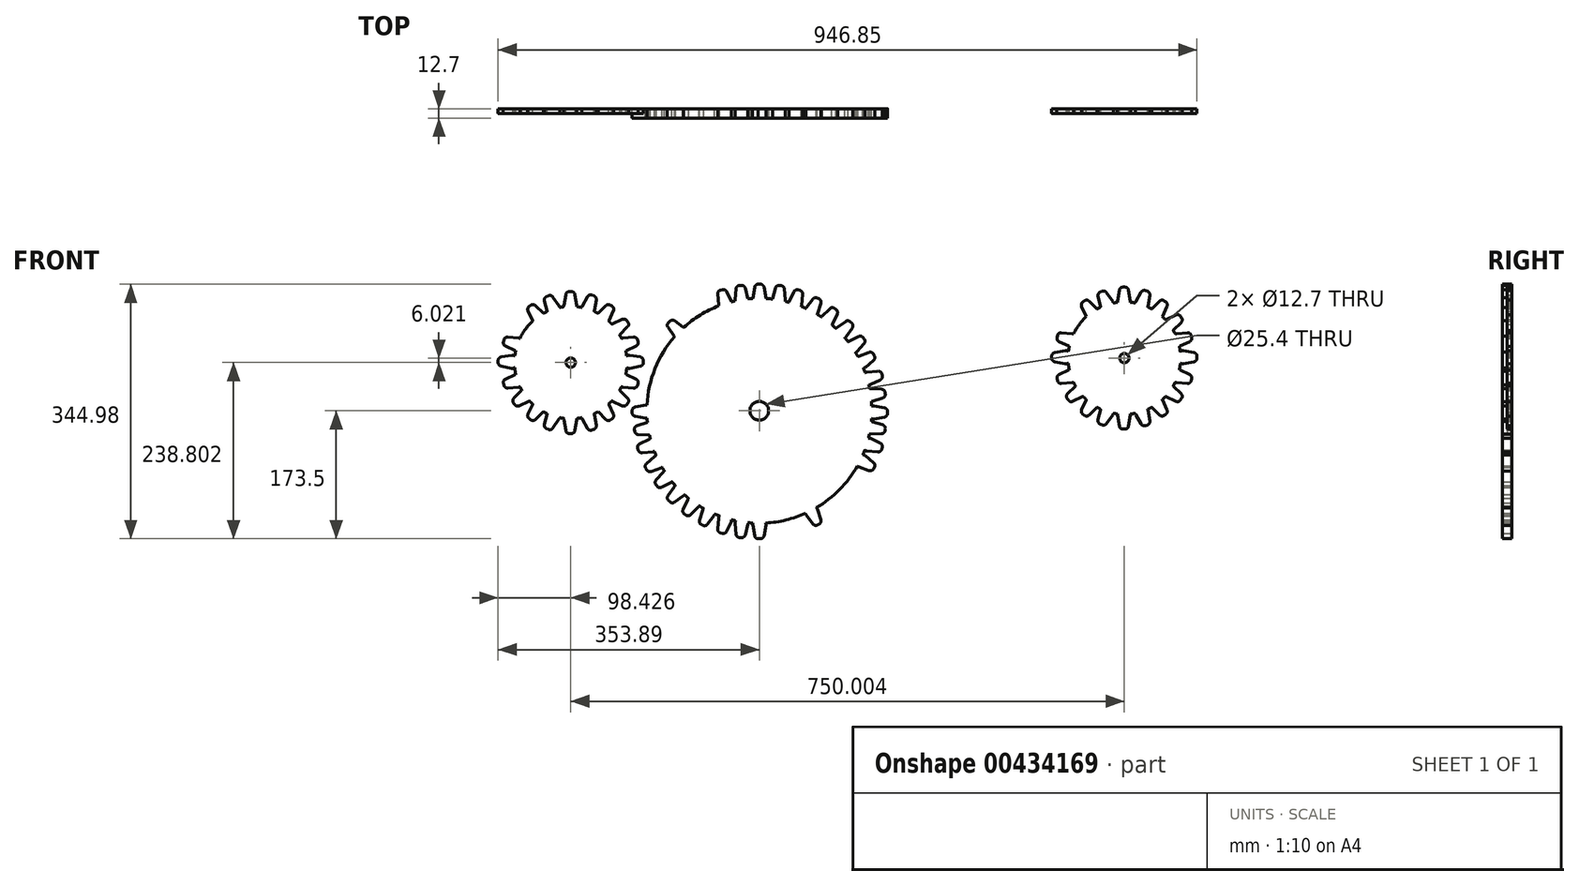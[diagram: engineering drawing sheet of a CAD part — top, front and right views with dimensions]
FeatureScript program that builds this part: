
annotation { "Feature Type Name" : "Feature", "Feature Type Description" : "" }
export const myFeature = defineFeature(function(context is Context, id is Id, definition is map)
    precondition{}
    {
        {
            var Q0;
            Q0=qCreatedBy(makeId("Front.planeOp"),FACE);
            var sketch = newSketch(context, id + "F0", { "sketchPlane" : qUnion([Q0])});
            skCircle(sketch, "E0", {"center": v(0, 0) * mm, "radius": 152.4 * mm});
            skCircle(sketch, "E1", {"center": v(0, 0) * mm, "radius": 12.7 * mm});
            skCircle(sketch, "E2", {"center": v(494.54, 71.32) * mm, "radius": 76.2 * mm});
            skCircle(sketch, "E3", {"center": v(494.54, 71.32) * mm, "radius": 6.35 * mm});
            skLineSegment(sketch, "E4", {"start": v(-3.93, 146.91) * mm, "end": v(3.69, 146.91) * mm});
            skLineSegment(sketch, "E5", {"start": v(-6.4, 167.28) * mm, "end": v(-8.94, 152.88) * mm});
            skPoint(sketch, "E6.visualSharp", {"position": v(5.4, 171.48) * mm});
            skPoint(sketch, "E7.visualSharp", {"position": v(-5.66, 171.48) * mm});
            skArc(sketch, "E7.filletArc", {"start": v(-1.37, 171.47) * mm, "mid": v(-4.65, 170.3) * mm, "end": v(-6.4, 167.28) * mm});
            skPoint(sketch, "E8.visualSharp", {"position": v(-9.99, 146.91) * mm});
            skArc(sketch, "E8.filletArc", {"start": v(-8.94, 152.88) * mm, "mid": v(-7.82, 148.73) * mm, "end": v(-3.93, 146.91) * mm});
            skPoint(sketch, "E9.visualSharp", {"position": v(9.74, 146.91) * mm});
            skLineSegment(sketch, "E10", {"start": v(10.44, 169.29) * mm, "end": v(10.23, 169.2) * mm});
            skPoint(sketch, "E11", {"position": v(18.24, 145.49) * mm});
            skLineSegment(sketch, "E12", {"start": v(22.3, 145.57) * mm, "end": v(29.9, 144.9) * mm});
            skLineSegment(sketch, "E13", {"start": v(35.4, 150.4) * mm, "end": v(34.12, 164.98) * mm});
            skLineSegment(sketch, "E14", {"start": v(29.5, 169.6) * mm, "end": v(26.98, 169.82) * mm});
            skLineSegment(sketch, "E15", {"start": v(21.63, 166.07) * mm, "end": v(17.84, 151.94) * mm});
            skArc(sketch, "E16.filletArc", {"start": v(34.12, 164.98) * mm, "mid": v(32.65, 168.13) * mm, "end": v(29.5, 169.6) * mm});
            skArc(sketch, "E17.filletArc", {"start": v(26.98, 169.82) * mm, "mid": v(23.62, 168.92) * mm, "end": v(21.63, 166.07) * mm});
            skArc(sketch, "E18.filletArc", {"start": v(17.84, 151.94) * mm, "mid": v(18.59, 147.71) * mm, "end": v(22.3, 145.57) * mm});
            skArc(sketch, "E19.filletArc", {"start": v(29.9, 144.9) * mm, "mid": v(33.93, 146.37) * mm, "end": v(35.4, 150.4) * mm});
            skLineSegment(sketch, "E20", {"start": v(43.8, 140.7) * mm, "end": v(51.17, 138.73) * mm});
            skLineSegment(sketch, "E21", {"start": v(57.54, 143.19) * mm, "end": v(58.82, 157.76) * mm});
            skLineSegment(sketch, "E22", {"start": v(55.07, 163.11) * mm, "end": v(52.62, 163.77) * mm});
            skLineSegment(sketch, "E23", {"start": v(46.7, 161) * mm, "end": v(40.52, 147.75) * mm});
            skArc(sketch, "E24.filletArc", {"start": v(58.82, 157.76) * mm, "mid": v(57.92, 161.12) * mm, "end": v(55.07, 163.11) * mm});
            skArc(sketch, "E25.filletArc", {"start": v(52.62, 163.77) * mm, "mid": v(49.16, 163.47) * mm, "end": v(46.7, 161) * mm});
            skArc(sketch, "E26.filletArc", {"start": v(40.52, 147.75) * mm, "mid": v(40.52, 143.46) * mm, "end": v(43.8, 140.7) * mm});
            skArc(sketch, "E27.filletArc", {"start": v(51.17, 138.73) * mm, "mid": v(55.4, 139.47) * mm, "end": v(57.54, 143.19) * mm});
            skLineSegment(sketch, "E28", {"start": v(65.39, 132.04) * mm, "end": v(71.8, 128.73) * mm});
            skLineSegment(sketch, "E29", {"start": v(78.98, 131.74) * mm, "end": v(83.32, 145.72) * mm});
            skLineSegment(sketch, "E30", {"start": v(80.79, 151.74) * mm, "end": v(78.89, 152.71) * mm});
            skLineSegment(sketch, "E31", {"start": v(72.52, 151.27) * mm, "end": v(63.67, 139.63) * mm});
            skArc(sketch, "E32.filletArc", {"start": v(83.32, 145.72) * mm, "mid": v(83.15, 149.19) * mm, "end": v(80.79, 151.74) * mm});
            skArc(sketch, "E33.filletArc", {"start": v(78.89, 152.71) * mm, "mid": v(75.44, 153.15) * mm, "end": v(72.52, 151.27) * mm});
            skArc(sketch, "E34.filletArc", {"start": v(63.67, 139.63) * mm, "mid": v(62.76, 135.43) * mm, "end": v(65.39, 132.04) * mm});
            skArc(sketch, "E35.filletArc", {"start": v(71.8, 128.73) * mm, "mid": v(76.1, 128.57) * mm, "end": v(78.98, 131.74) * mm});
            skLineSegment(sketch, "E36", {"start": v(85.6, 120.15) * mm, "end": v(91.84, 115.78) * mm});
            skLineSegment(sketch, "E37", {"start": v(99.36, 117.8) * mm, "end": v(105.54, 131.05) * mm});
            skLineSegment(sketch, "E38", {"start": v(103.85, 137.36) * mm, "end": v(101.77, 138.82) * mm});
            skLineSegment(sketch, "E39", {"start": v(95.26, 138.25) * mm, "end": v(84.92, 127.9) * mm});
            skArc(sketch, "E40.filletArc", {"start": v(105.54, 131.05) * mm, "mid": v(105.84, 134.51) * mm, "end": v(103.85, 137.36) * mm});
            skArc(sketch, "E41.filletArc", {"start": v(101.77, 138.82) * mm, "mid": v(98.41, 139.72) * mm, "end": v(95.26, 138.25) * mm});
            skArc(sketch, "E42.filletArc", {"start": v(84.92, 127.9) * mm, "mid": v(83.45, 123.87) * mm, "end": v(85.6, 120.15) * mm});
            skArc(sketch, "E43.filletArc", {"start": v(91.84, 115.78) * mm, "mid": v(96.07, 115.03) * mm, "end": v(99.36, 117.8) * mm});
            skLineSegment(sketch, "E44", {"start": v(104.46, 105.05) * mm, "end": v(109.86, 99.65) * mm});
            skLineSegment(sketch, "E45", {"start": v(117.62, 100.33) * mm, "end": v(125.88, 112.13) * mm});
            skLineSegment(sketch, "E46", {"start": v(125.31, 118.63) * mm, "end": v(123.45, 120.5) * mm});
            skLineSegment(sketch, "E47", {"start": v(116.94, 121.06) * mm, "end": v(105.14, 112.8) * mm});
            skArc(sketch, "E48.filletArc", {"start": v(125.88, 112.13) * mm, "mid": v(126.78, 115.48) * mm, "end": v(125.31, 118.63) * mm});
            skArc(sketch, "E49.filletArc", {"start": v(123.45, 120.5) * mm, "mid": v(120.3, 121.96) * mm, "end": v(116.94, 121.06) * mm});
            skArc(sketch, "E50.filletArc", {"start": v(105.14, 112.8) * mm, "mid": v(103, 109.08) * mm, "end": v(104.46, 105.05) * mm});
            skArc(sketch, "E51.filletArc", {"start": v(109.86, 99.65) * mm, "mid": v(113.9, 98.18) * mm, "end": v(117.62, 100.33) * mm});
            skLineSegment(sketch, "E52", {"start": v(119.6, 86.31) * mm, "end": v(124.28, 80.3) * mm});
            skLineSegment(sketch, "E53", {"start": v(132.05, 80) * mm, "end": v(141.88, 90.84) * mm});
            skLineSegment(sketch, "E54", {"start": v(142.12, 97.37) * mm, "end": v(140.57, 99.37) * mm});
            skLineSegment(sketch, "E55", {"start": v(134.18, 100.75) * mm, "end": v(121.25, 93.92) * mm});
            skArc(sketch, "E56.filletArc", {"start": v(141.88, 90.84) * mm, "mid": v(143.19, 94.06) * mm, "end": v(142.12, 97.37) * mm});
            skArc(sketch, "E57.filletArc", {"start": v(140.57, 99.37) * mm, "mid": v(137.62, 101.22) * mm, "end": v(134.18, 100.75) * mm});
            skArc(sketch, "E58.filletArc", {"start": v(121.25, 93.92) * mm, "mid": v(118.65, 90.5) * mm, "end": v(119.6, 86.31) * mm});
            skArc(sketch, "E59.filletArc", {"start": v(124.28, 80.3) * mm, "mid": v(128.1, 78.33) * mm, "end": v(132.05, 80) * mm});
            skLineSegment(sketch, "E60", {"start": v(132.03, 66.8) * mm, "end": v(135.84, 60.2) * mm});
            skLineSegment(sketch, "E61", {"start": v(143.5, 58.84) * mm, "end": v(154.71, 68.24) * mm});
            skLineSegment(sketch, "E62", {"start": v(155.85, 74.68) * mm, "end": v(154.58, 76.88) * mm});
            skLineSegment(sketch, "E63", {"start": v(148.44, 79.1) * mm, "end": v(134.7, 74.1) * mm});
            skArc(sketch, "E64.filletArc", {"start": v(154.71, 68.24) * mm, "mid": v(156.45, 71.25) * mm, "end": v(155.85, 74.68) * mm});
            skArc(sketch, "E65.filletArc", {"start": v(154.58, 76.88) * mm, "mid": v(151.92, 79.1) * mm, "end": v(148.44, 79.1) * mm});
            skArc(sketch, "E66.filletArc", {"start": v(134.7, 74.1) * mm, "mid": v(131.66, 71.07) * mm, "end": v(132.03, 66.8) * mm});
            skArc(sketch, "E67.filletArc", {"start": v(135.84, 60.2) * mm, "mid": v(139.36, 57.73) * mm, "end": v(143.5, 58.84) * mm});
            skLineSegment(sketch, "E68", {"start": v(141.48, 46.14) * mm, "end": v(143.45, 38.78) * mm});
            skLineSegment(sketch, "E69", {"start": v(150.5, 35.5) * mm, "end": v(163.76, 41.68) * mm});
            skLineSegment(sketch, "E70", {"start": v(166.52, 47.6) * mm, "end": v(165.86, 50.05) * mm});
            skLineSegment(sketch, "E71", {"start": v(160.51, 53.8) * mm, "end": v(145.94, 52.52) * mm});
            skArc(sketch, "E72.filletArc", {"start": v(163.76, 41.68) * mm, "mid": v(166.22, 44.13) * mm, "end": v(166.52, 47.6) * mm});
            skArc(sketch, "E73.filletArc", {"start": v(165.86, 50.05) * mm, "mid": v(163.87, 52.9) * mm, "end": v(160.51, 53.8) * mm});
            skArc(sketch, "E74.filletArc", {"start": v(145.94, 52.52) * mm, "mid": v(142.22, 50.37) * mm, "end": v(141.48, 46.14) * mm});
            skArc(sketch, "E75.filletArc", {"start": v(143.45, 38.78) * mm, "mid": v(146.2, 35.5) * mm, "end": v(150.5, 35.5) * mm});
            skLineSegment(sketch, "E76", {"start": v(145.77, 24.1) * mm, "end": v(146.7, 16.95) * mm});
            skLineSegment(sketch, "E77", {"start": v(153.25, 12.76) * mm, "end": v(167.2, 17.14) * mm});
            skLineSegment(sketch, "E78", {"start": v(170.73, 22.64) * mm, "end": v(170.45, 24.74) * mm});
            skLineSegment(sketch, "E79", {"start": v(165.65, 29.16) * mm, "end": v(151.03, 29.82) * mm});
            skArc(sketch, "E80.filletArc", {"start": v(167.2, 17.14) * mm, "mid": v(169.97, 19.25) * mm, "end": v(170.73, 22.64) * mm});
            skArc(sketch, "E81.filletArc", {"start": v(170.45, 24.74) * mm, "mid": v(168.85, 27.83) * mm, "end": v(165.65, 29.16) * mm});
            skArc(sketch, "E82.filletArc", {"start": v(151.03, 29.82) * mm, "mid": v(147.06, 28.18) * mm, "end": v(145.77, 24.1) * mm});
            skArc(sketch, "E83.filletArc", {"start": v(146.7, 16.95) * mm, "mid": v(149, 13.33) * mm, "end": v(153.25, 12.76) * mm});
            skLineSegment(sketch, "E84.MirrorCS", {"start": v(-1.37, 171.47) * mm, "end": v(1.4, 171.48) * mm});
            skLineSegment(sketch, "E85.MirrorCS", {"start": v(-10.44, 169.29) * mm, "end": v(-10.23, 169.2) * mm});
            skLineSegment(sketch, "E86.MirrorCS", {"start": v(3.93, 146.91) * mm, "end": v(-3.69, 146.91) * mm});
            skLineSegment(sketch, "E87.MirrorCS", {"start": v(6.4, 167.28) * mm, "end": v(8.94, 152.88) * mm});
            skArc(sketch, "E88.MirrorCS", {"start": v(1.4, 171.48) * mm, "mid": v(4.66, 170.29) * mm, "end": v(6.4, 167.28) * mm});
            skArc(sketch, "E89.MirrorCS", {"start": v(8.94, 152.88) * mm, "mid": v(7.82, 148.73) * mm, "end": v(3.93, 146.91) * mm});
            skPoint(sketch, "E90.MirrorP", {"position": v(-5.4, 171.48) * mm});
            skPoint(sketch, "E91.MirrorP", {"position": v(5.66, 171.48) * mm});
            skPoint(sketch, "E92.MirrorP", {"position": v(9.99, 146.91) * mm});
            skPoint(sketch, "E93.MirrorP", {"position": v(-9.74, 146.91) * mm});
            skLineSegment(sketch, "E94", {"start": v(149.19, 1.53) * mm, "end": v(149.19, -6.1) * mm});
            skLineSegment(sketch, "E95", {"start": v(155.15, -11.1) * mm, "end": v(169.56, -8.56) * mm});
            skLineSegment(sketch, "E96", {"start": v(173.75, -3.55) * mm, "end": v(173.75, -1.01) * mm});
            skLineSegment(sketch, "E97", {"start": v(169.56, 4) * mm, "end": v(155.15, 6.53) * mm});
            skArc(sketch, "E98.filletArc", {"start": v(169.56, -8.56) * mm, "mid": v(172.57, -6.82) * mm, "end": v(173.75, -3.55) * mm});
            skArc(sketch, "E99.filletArc", {"start": v(173.75, -1.01) * mm, "mid": v(172.57, 2.25) * mm, "end": v(169.56, 4) * mm});
            skArc(sketch, "E100.filletArc", {"start": v(155.15, 6.53) * mm, "mid": v(151, 5.42) * mm, "end": v(149.19, 1.53) * mm});
            skArc(sketch, "E101.filletArc", {"start": v(149.19, -6.1) * mm, "mid": v(151, -9.98) * mm, "end": v(155.15, -11.1) * mm});
            skLineSegment(sketch, "E102", {"start": v(494.54, 185.24) * mm, "end": v(494.54, -63.97) * mm});
            skLineSegment(sketch, "E103", {"start": v(395, 71.32) * mm, "end": v(592.82, 71.32) * mm});
            skLineSegment(sketch, "E104", {"start": v(490.18, 142.96) * mm, "end": v(497.8, 142.96) * mm});
            skLineSegment(sketch, "E105", {"start": v(502.8, 148.92) * mm, "end": v(500.26, 163.33) * mm});
            skLineSegment(sketch, "E106", {"start": v(495.26, 167.52) * mm, "end": v(492.72, 167.52) * mm});
            skLineSegment(sketch, "E107", {"start": v(487.72, 163.33) * mm, "end": v(485.18, 148.92) * mm});
            skArc(sketch, "E108.filletArc", {"start": v(500.26, 163.33) * mm, "mid": v(498.52, 166.34) * mm, "end": v(495.26, 167.52) * mm});
            skArc(sketch, "E109.filletArc", {"start": v(492.72, 167.52) * mm, "mid": v(489.45, 166.34) * mm, "end": v(487.72, 163.33) * mm});
            skArc(sketch, "E110.filletArc", {"start": v(485.18, 148.92) * mm, "mid": v(486.29, 144.77) * mm, "end": v(490.18, 142.96) * mm});
            skArc(sketch, "E111.filletArc", {"start": v(497.8, 142.96) * mm, "mid": v(501.69, 144.77) * mm, "end": v(502.8, 148.92) * mm});
            skLineSegment(sketch, "E112", {"start": v(512.62, 140.59) * mm, "end": v(519.78, 137.98) * mm});
            skLineSegment(sketch, "E113", {"start": v(526.52, 141.87) * mm, "end": v(529.06, 156.28) * mm});
            skLineSegment(sketch, "E114", {"start": v(525.8, 161.93) * mm, "end": v(523.4, 162.8) * mm});
            skLineSegment(sketch, "E115", {"start": v(517.27, 160.57) * mm, "end": v(509.95, 147.9) * mm});
            skArc(sketch, "E116.filletArc", {"start": v(529.06, 156.28) * mm, "mid": v(528.45, 159.7) * mm, "end": v(525.8, 161.93) * mm});
            skArc(sketch, "E117.filletArc", {"start": v(523.4, 162.8) * mm, "mid": v(519.93, 162.8) * mm, "end": v(517.27, 160.57) * mm});
            skArc(sketch, "E118.filletArc", {"start": v(509.95, 147.9) * mm, "mid": v(509.58, 143.62) * mm, "end": v(512.62, 140.59) * mm});
            skArc(sketch, "E119.filletArc", {"start": v(519.78, 137.98) * mm, "mid": v(524.05, 138.35) * mm, "end": v(526.52, 141.87) * mm});
            skLineSegment(sketch, "E120", {"start": v(532.43, 130.27) * mm, "end": v(538.67, 125.9) * mm});
            skLineSegment(sketch, "E121", {"start": v(546.2, 127.91) * mm, "end": v(552.37, 141.17) * mm});
            skLineSegment(sketch, "E122", {"start": v(550.68, 147.48) * mm, "end": v(548.6, 148.94) * mm});
            skLineSegment(sketch, "E123", {"start": v(542.1, 148.37) * mm, "end": v(531.75, 138.02) * mm});
            skArc(sketch, "E124.filletArc", {"start": v(552.37, 141.17) * mm, "mid": v(552.68, 144.63) * mm, "end": v(550.68, 147.48) * mm});
            skArc(sketch, "E125.filletArc", {"start": v(548.6, 148.94) * mm, "mid": v(545.25, 149.84) * mm, "end": v(542.1, 148.37) * mm});
            skArc(sketch, "E126.filletArc", {"start": v(531.75, 138.02) * mm, "mid": v(530.29, 133.99) * mm, "end": v(532.43, 130.27) * mm});
            skArc(sketch, "E127.filletArc", {"start": v(538.67, 125.9) * mm, "mid": v(542.9, 125.15) * mm, "end": v(546.2, 127.91) * mm});
            skLineSegment(sketch, "E128", {"start": v(549.03, 116.13) * mm, "end": v(553.4, 109.89) * mm});
            skLineSegment(sketch, "E129", {"start": v(561.15, 109.2) * mm, "end": v(571.5, 119.55) * mm});
            skLineSegment(sketch, "E130", {"start": v(572.06, 126.06) * mm, "end": v(570.6, 128.14) * mm});
            skLineSegment(sketch, "E131", {"start": v(564.3, 129.83) * mm, "end": v(551.04, 123.64) * mm});
            skArc(sketch, "E132.filletArc", {"start": v(571.5, 119.55) * mm, "mid": v(572.96, 122.7) * mm, "end": v(572.06, 126.06) * mm});
            skArc(sketch, "E133.filletArc", {"start": v(570.6, 128.14) * mm, "mid": v(567.76, 130.13) * mm, "end": v(564.3, 129.83) * mm});
            skArc(sketch, "E134.filletArc", {"start": v(551.04, 123.64) * mm, "mid": v(548.28, 120.36) * mm, "end": v(549.03, 116.13) * mm});
            skArc(sketch, "E135.filletArc", {"start": v(553.4, 109.89) * mm, "mid": v(557.12, 107.74) * mm, "end": v(561.15, 109.2) * mm});
            skLineSegment(sketch, "E136", {"start": v(560.7, 98.14) * mm, "end": v(562.67, 90.78) * mm});
            skLineSegment(sketch, "E137", {"start": v(569.73, 87.5) * mm, "end": v(582.98, 93.68) * mm});
            skLineSegment(sketch, "E138", {"start": v(585.74, 99.6) * mm, "end": v(585.09, 102.05) * mm});
            skLineSegment(sketch, "E139", {"start": v(579.74, 105.8) * mm, "end": v(565.17, 104.52) * mm});
            skArc(sketch, "E140.filletArc", {"start": v(582.98, 93.68) * mm, "mid": v(585.44, 96.13) * mm, "end": v(585.74, 99.6) * mm});
            skArc(sketch, "E141.filletArc", {"start": v(585.09, 102.05) * mm, "mid": v(583.1, 104.9) * mm, "end": v(579.74, 105.8) * mm});
            skArc(sketch, "E142.filletArc", {"start": v(565.17, 104.52) * mm, "mid": v(561.45, 102.37) * mm, "end": v(560.7, 98.14) * mm});
            skArc(sketch, "E143.filletArc", {"start": v(562.67, 90.78) * mm, "mid": v(565.43, 87.5) * mm, "end": v(569.73, 87.5) * mm});
            skLineSegment(sketch, "E144", {"start": v(568.33, 76.14) * mm, "end": v(568.44, 68.52) * mm});
            skLineSegment(sketch, "E145", {"start": v(574.47, 63.6) * mm, "end": v(588.84, 66.35) * mm});
            skLineSegment(sketch, "E146", {"start": v(592.96, 71.41) * mm, "end": v(592.93, 73.95) * mm});
            skLineSegment(sketch, "E147", {"start": v(588.66, 78.9) * mm, "end": v(574.22, 81.23) * mm});
            skArc(sketch, "E148.filletArc", {"start": v(588.84, 66.35) * mm, "mid": v(591.82, 68.13) * mm, "end": v(592.96, 71.41) * mm});
            skArc(sketch, "E149.filletArc", {"start": v(592.93, 73.95) * mm, "mid": v(591.7, 77.2) * mm, "end": v(588.66, 78.9) * mm});
            skArc(sketch, "E150.filletArc", {"start": v(574.22, 81.23) * mm, "mid": v(570.09, 80.06) * mm, "end": v(568.33, 76.14) * mm});
            skArc(sketch, "E151.filletArc", {"start": v(568.44, 68.52) * mm, "mid": v(570.3, 64.66) * mm, "end": v(574.47, 63.6) * mm});
            skLineSegment(sketch, "E152.MirrorCS", {"start": v(396.12, 71.41) * mm, "end": v(396.15, 73.95) * mm});
            skLineSegment(sketch, "E153.MirrorCS", {"start": v(403.34, 99.6) * mm, "end": v(404, 102.05) * mm});
            skArc(sketch, "E154.MirrorCS", {"start": v(396.15, 73.95) * mm, "mid": v(397.39, 77.2) * mm, "end": v(400.42, 78.9) * mm});
            skArc(sketch, "E155.MirrorCS", {"start": v(418.47, 128.14) * mm, "mid": v(421.32, 130.13) * mm, "end": v(424.78, 129.83) * mm});
            skArc(sketch, "E156.MirrorCS", {"start": v(414.86, 81.23) * mm, "mid": v(419, 80.06) * mm, "end": v(420.75, 76.14) * mm});
            skArc(sketch, "E157.MirrorCS", {"start": v(438.04, 123.64) * mm, "mid": v(440.8, 120.36) * mm, "end": v(440.05, 116.13) * mm});
            skArc(sketch, "E158.MirrorCS", {"start": v(435.68, 109.89) * mm, "mid": v(431.96, 107.74) * mm, "end": v(427.93, 109.2) * mm});
            skLineSegment(sketch, "E159.MirrorCS", {"start": v(456.65, 130.27) * mm, "end": v(450.4, 125.9) * mm});
            skLineSegment(sketch, "E160.MirrorCS", {"start": v(428.38, 98.14) * mm, "end": v(426.4, 90.78) * mm});
            skLineSegment(sketch, "E161.MirrorCS", {"start": v(438.4, 147.48) * mm, "end": v(440.48, 148.94) * mm});
            skArc(sketch, "E162.MirrorCS", {"start": v(406.1, 93.68) * mm, "mid": v(403.64, 96.13) * mm, "end": v(403.34, 99.6) * mm});
            skArc(sketch, "E163.MirrorCS", {"start": v(436.7, 141.17) * mm, "mid": v(436.4, 144.63) * mm, "end": v(438.4, 147.48) * mm});
            skArc(sketch, "E164.MirrorCS", {"start": v(404, 102.05) * mm, "mid": v(405.99, 104.9) * mm, "end": v(409.34, 105.8) * mm});
            skArc(sketch, "E165.MirrorCS", {"start": v(440.48, 148.94) * mm, "mid": v(443.83, 149.84) * mm, "end": v(446.98, 148.37) * mm});
            skArc(sketch, "E166.MirrorCS", {"start": v(457.33, 138.02) * mm, "mid": v(458.8, 133.99) * mm, "end": v(456.65, 130.27) * mm});
            skArc(sketch, "E167.MirrorCS", {"start": v(423.91, 104.52) * mm, "mid": v(427.63, 102.37) * mm, "end": v(428.38, 98.14) * mm});
            skArc(sketch, "E168.MirrorCS", {"start": v(450.4, 125.9) * mm, "mid": v(446.18, 125.15) * mm, "end": v(442.89, 127.91) * mm});
            skArc(sketch, "E169.MirrorCS", {"start": v(426.4, 90.78) * mm, "mid": v(423.65, 87.5) * mm, "end": v(419.35, 87.5) * mm});
            skLineSegment(sketch, "E170.MirrorCS", {"start": v(440.05, 116.13) * mm, "end": v(435.68, 109.89) * mm});
            skLineSegment(sketch, "E171.MirrorCS", {"start": v(420.75, 76.14) * mm, "end": v(420.64, 68.52) * mm});
            skLineSegment(sketch, "E172.MirrorCS", {"start": v(417.02, 126.06) * mm, "end": v(418.47, 128.14) * mm});
            skArc(sketch, "E173.MirrorCS", {"start": v(417.58, 119.55) * mm, "mid": v(416.12, 122.7) * mm, "end": v(417.02, 126.06) * mm});
            skArc(sketch, "E174.MirrorCS", {"start": v(400.24, 66.35) * mm, "mid": v(397.26, 68.13) * mm, "end": v(396.12, 71.41) * mm});
            skLineSegment(sketch, "E175.MirrorCS", {"start": v(424.78, 129.83) * mm, "end": v(438.04, 123.64) * mm});
            skLineSegment(sketch, "E176.MirrorCS", {"start": v(400.42, 78.9) * mm, "end": v(414.86, 81.23) * mm});
            skArc(sketch, "E177.MirrorCS", {"start": v(420.64, 68.52) * mm, "mid": v(418.77, 64.66) * mm, "end": v(414.61, 63.6) * mm});
            skLineSegment(sketch, "E178.MirrorCS", {"start": v(419.35, 87.5) * mm, "end": v(406.1, 93.68) * mm});
            skLineSegment(sketch, "E179.MirrorCS", {"start": v(442.89, 127.91) * mm, "end": v(436.7, 141.17) * mm});
            skLineSegment(sketch, "E180.MirrorCS", {"start": v(409.34, 105.8) * mm, "end": v(423.91, 104.52) * mm});
            skLineSegment(sketch, "E181.MirrorCS", {"start": v(446.98, 148.37) * mm, "end": v(457.33, 138.02) * mm});
            skLineSegment(sketch, "E182.MirrorCS", {"start": v(427.93, 109.2) * mm, "end": v(417.58, 119.55) * mm});
            skLineSegment(sketch, "E183.MirrorCS", {"start": v(414.61, 63.6) * mm, "end": v(400.24, 66.35) * mm});
            skLineSegment(sketch, "E184", {"start": v(469.82, 137.42) * mm, "end": v(476.73, 140.64) * mm});
            skLineSegment(sketch, "E185", {"start": v(478.74, 148.16) * mm, "end": v(470.35, 160.14) * mm});
            skLineSegment(sketch, "E186", {"start": v(464.04, 161.83) * mm, "end": v(461.74, 160.76) * mm});
            skLineSegment(sketch, "E187", {"start": v(458.98, 154.84) * mm, "end": v(462.77, 140.71) * mm});
            skArc(sketch, "E188.filletArc", {"start": v(470.35, 160.14) * mm, "mid": v(467.5, 162.14) * mm, "end": v(464.04, 161.83) * mm});
            skArc(sketch, "E189.filletArc", {"start": v(461.74, 160.76) * mm, "mid": v(459.28, 158.3) * mm, "end": v(458.98, 154.84) * mm});
            skArc(sketch, "E190.filletArc", {"start": v(462.77, 140.71) * mm, "mid": v(465.53, 137.42) * mm, "end": v(469.82, 137.42) * mm});
            skArc(sketch, "E191.filletArc", {"start": v(476.73, 140.64) * mm, "mid": v(479.49, 143.93) * mm, "end": v(478.74, 148.16) * mm});
            skLineSegment(sketch, "E192.MirrorCS", {"start": v(403.34, 43.05) * mm, "end": v(404, 40.6) * mm});
            skLineSegment(sketch, "E193.MirrorCS", {"start": v(585.74, 43.05) * mm, "end": v(585.09, 40.6) * mm});
            skLineSegment(sketch, "E194.MirrorCS", {"start": v(550.68, -4.83) * mm, "end": v(548.6, -6.3) * mm});
            skLineSegment(sketch, "E195.MirrorCS", {"start": v(495.26, -24.88) * mm, "end": v(492.72, -24.88) * mm});
            skLineSegment(sketch, "E196.MirrorCS", {"start": v(464.04, -19.19) * mm, "end": v(461.74, -18.11) * mm});
            skLineSegment(sketch, "E197.MirrorCS", {"start": v(417.02, 16.6) * mm, "end": v(418.47, 14.51) * mm});
            skLineSegment(sketch, "E198.MirrorCS", {"start": v(438.4, -4.83) * mm, "end": v(440.48, -6.3) * mm});
            skLineSegment(sketch, "E199.MirrorCS", {"start": v(572.06, 16.6) * mm, "end": v(570.6, 14.51) * mm});
            skLineSegment(sketch, "E200.MirrorCS", {"start": v(525.8, -19.29) * mm, "end": v(523.4, -20.15) * mm});
            skArc(sketch, "E201.MirrorCS", {"start": v(582.98, 48.97) * mm, "mid": v(585.44, 46.51) * mm, "end": v(585.74, 43.05) * mm});
            skArc(sketch, "E202.MirrorCS", {"start": v(571.5, 23.1) * mm, "mid": v(572.96, 19.95) * mm, "end": v(572.06, 16.6) * mm});
            skArc(sketch, "E203.MirrorCS", {"start": v(519.78, 4.67) * mm, "mid": v(524.05, 4.3) * mm, "end": v(526.52, 0.78) * mm});
            skArc(sketch, "E204.MirrorCS", {"start": v(423.91, 38.13) * mm, "mid": v(427.63, 40.27) * mm, "end": v(428.38, 44.5) * mm});
            skArc(sketch, "E205.MirrorCS", {"start": v(553.4, 32.76) * mm, "mid": v(557.12, 34.9) * mm, "end": v(561.15, 33.44) * mm});
            skLineSegment(sketch, "E206.MirrorCS", {"start": v(560.7, 44.5) * mm, "end": v(562.67, 51.86) * mm});
            skLineSegment(sketch, "E207.MirrorCS", {"start": v(532.43, 12.38) * mm, "end": v(538.67, 16.75) * mm});
            skLineSegment(sketch, "E208.MirrorCS", {"start": v(490.18, -0.31) * mm, "end": v(497.8, -0.31) * mm});
            skArc(sketch, "E209.MirrorCS", {"start": v(450.4, 16.75) * mm, "mid": v(446.18, 17.5) * mm, "end": v(442.89, 14.73) * mm});
            skLineSegment(sketch, "E210.MirrorCS", {"start": v(469.82, 5.22) * mm, "end": v(476.73, 2) * mm});
            skLineSegment(sketch, "E211.MirrorCS", {"start": v(569.73, 55.15) * mm, "end": v(582.98, 48.97) * mm});
            skLineSegment(sketch, "E212.MirrorCS", {"start": v(546.2, 14.73) * mm, "end": v(552.37, 1.47) * mm});
            skLineSegment(sketch, "E213.MirrorCS", {"start": v(502.8, -6.27) * mm, "end": v(500.26, -20.68) * mm});
            skLineSegment(sketch, "E214.MirrorCS", {"start": v(478.74, -5.51) * mm, "end": v(470.35, -17.5) * mm});
            skArc(sketch, "E215.MirrorCS", {"start": v(426.4, 51.86) * mm, "mid": v(423.65, 55.15) * mm, "end": v(419.35, 55.15) * mm});
            skLineSegment(sketch, "E216.MirrorCS", {"start": v(440.05, 26.52) * mm, "end": v(435.68, 32.76) * mm});
            skArc(sketch, "E217.MirrorCS", {"start": v(418.47, 14.51) * mm, "mid": v(421.32, 12.52) * mm, "end": v(424.78, 12.82) * mm});
            skLineSegment(sketch, "E218.MirrorCS", {"start": v(579.74, 36.85) * mm, "end": v(565.17, 38.13) * mm});
            skLineSegment(sketch, "E219.MirrorCS", {"start": v(542.1, -5.72) * mm, "end": v(531.75, 4.62) * mm});
            skLineSegment(sketch, "E220.MirrorCS", {"start": v(487.72, -20.68) * mm, "end": v(485.18, -6.27) * mm});
            skLineSegment(sketch, "E221.MirrorCS", {"start": v(458.98, -12.2) * mm, "end": v(462.77, 1.93) * mm});
            skArc(sketch, "E222.MirrorCS", {"start": v(470.35, -17.5) * mm, "mid": v(467.5, -19.49) * mm, "end": v(464.04, -19.19) * mm});
            skArc(sketch, "E223.MirrorCS", {"start": v(552.37, 1.47) * mm, "mid": v(552.68, -1.99) * mm, "end": v(550.68, -4.83) * mm});
            skArc(sketch, "E224.MirrorCS", {"start": v(500.26, -20.68) * mm, "mid": v(498.52, -23.69) * mm, "end": v(495.26, -24.88) * mm});
            skArc(sketch, "E225.MirrorCS", {"start": v(461.74, -18.11) * mm, "mid": v(459.28, -15.66) * mm, "end": v(458.98, -12.2) * mm});
            skArc(sketch, "E226.MirrorCS", {"start": v(417.58, 23.1) * mm, "mid": v(416.12, 19.95) * mm, "end": v(417.02, 16.6) * mm});
            skArc(sketch, "E227.MirrorCS", {"start": v(438.04, 19) * mm, "mid": v(440.8, 22.3) * mm, "end": v(440.05, 26.52) * mm});
            skArc(sketch, "E228.MirrorCS", {"start": v(585.09, 40.6) * mm, "mid": v(583.1, 37.75) * mm, "end": v(579.74, 36.85) * mm});
            skArc(sketch, "E229.MirrorCS", {"start": v(548.6, -6.3) * mm, "mid": v(545.25, -7.19) * mm, "end": v(542.1, -5.72) * mm});
            skArc(sketch, "E230.MirrorCS", {"start": v(492.72, -24.88) * mm, "mid": v(489.45, -23.69) * mm, "end": v(487.72, -20.68) * mm});
            skArc(sketch, "E231.MirrorCS", {"start": v(531.75, 4.62) * mm, "mid": v(530.29, 8.66) * mm, "end": v(532.43, 12.38) * mm});
            skArc(sketch, "E232.MirrorCS", {"start": v(485.18, -6.27) * mm, "mid": v(486.29, -2.13) * mm, "end": v(490.18, -0.31) * mm});
            skArc(sketch, "E233.MirrorCS", {"start": v(435.68, 32.76) * mm, "mid": v(431.96, 34.9) * mm, "end": v(427.93, 33.44) * mm});
            skArc(sketch, "E234.MirrorCS", {"start": v(462.77, 1.93) * mm, "mid": v(465.53, 5.22) * mm, "end": v(469.82, 5.22) * mm});
            skArc(sketch, "E235.MirrorCS", {"start": v(565.17, 38.13) * mm, "mid": v(561.45, 40.27) * mm, "end": v(560.7, 44.5) * mm});
            skArc(sketch, "E236.MirrorCS", {"start": v(538.67, 16.75) * mm, "mid": v(542.9, 17.5) * mm, "end": v(546.2, 14.73) * mm});
            skArc(sketch, "E237.MirrorCS", {"start": v(497.8, -0.31) * mm, "mid": v(501.69, -2.13) * mm, "end": v(502.8, -6.27) * mm});
            skLineSegment(sketch, "E238.MirrorCS", {"start": v(456.65, 12.38) * mm, "end": v(450.4, 16.75) * mm});
            skArc(sketch, "E239.MirrorCS", {"start": v(562.67, 51.86) * mm, "mid": v(565.43, 55.15) * mm, "end": v(569.73, 55.15) * mm});
            skLineSegment(sketch, "E240.MirrorCS", {"start": v(424.78, 12.82) * mm, "end": v(438.04, 19) * mm});
            skArc(sketch, "E241.MirrorCS", {"start": v(476.73, 2) * mm, "mid": v(479.49, -1.29) * mm, "end": v(478.74, -5.51) * mm});
            skLineSegment(sketch, "E242.MirrorCS", {"start": v(549.03, 26.52) * mm, "end": v(553.4, 32.76) * mm});
            skLineSegment(sketch, "E243.MirrorCS", {"start": v(512.62, 2.06) * mm, "end": v(519.78, 4.67) * mm});
            skLineSegment(sketch, "E244.MirrorCS", {"start": v(428.38, 44.5) * mm, "end": v(426.4, 51.86) * mm});
            skLineSegment(sketch, "E245.MirrorCS", {"start": v(561.15, 33.44) * mm, "end": v(571.5, 23.1) * mm});
            skLineSegment(sketch, "E246.MirrorCS", {"start": v(526.52, 0.78) * mm, "end": v(529.06, -13.63) * mm});
            skArc(sketch, "E247.MirrorCS", {"start": v(406.1, 48.97) * mm, "mid": v(403.64, 46.51) * mm, "end": v(403.34, 43.05) * mm});
            skLineSegment(sketch, "E248.MirrorCS", {"start": v(419.35, 55.15) * mm, "end": v(406.1, 48.97) * mm});
            skLineSegment(sketch, "E249.MirrorCS", {"start": v(564.3, 12.82) * mm, "end": v(551.04, 19) * mm});
            skLineSegment(sketch, "E250.MirrorCS", {"start": v(517.27, -17.92) * mm, "end": v(509.95, -5.25) * mm});
            skArc(sketch, "E251.MirrorCS", {"start": v(436.7, 1.47) * mm, "mid": v(436.4, -1.99) * mm, "end": v(438.4, -4.83) * mm});
            skLineSegment(sketch, "E252.MirrorCS", {"start": v(442.89, 14.73) * mm, "end": v(436.7, 1.47) * mm});
            skArc(sketch, "E253.MirrorCS", {"start": v(551.04, 19) * mm, "mid": v(548.28, 22.3) * mm, "end": v(549.03, 26.52) * mm});
            skArc(sketch, "E254.MirrorCS", {"start": v(509.95, -5.25) * mm, "mid": v(509.58, -0.98) * mm, "end": v(512.62, 2.06) * mm});
            skArc(sketch, "E255.MirrorCS", {"start": v(570.6, 14.51) * mm, "mid": v(567.76, 12.52) * mm, "end": v(564.3, 12.82) * mm});
            skArc(sketch, "E256.MirrorCS", {"start": v(523.4, -20.15) * mm, "mid": v(519.93, -20.15) * mm, "end": v(517.27, -17.92) * mm});
            skLineSegment(sketch, "E257.MirrorCS", {"start": v(427.93, 33.44) * mm, "end": v(417.58, 23.1) * mm});
            skLineSegment(sketch, "E258.MirrorCS", {"start": v(446.98, -5.72) * mm, "end": v(457.33, 4.62) * mm});
            skArc(sketch, "E259.MirrorCS", {"start": v(440.48, -6.3) * mm, "mid": v(443.83, -7.19) * mm, "end": v(446.98, -5.72) * mm});
            skLineSegment(sketch, "E260.MirrorCS", {"start": v(409.34, 36.85) * mm, "end": v(423.91, 38.13) * mm});
            skArc(sketch, "E261.MirrorCS", {"start": v(529.06, -13.63) * mm, "mid": v(528.45, -17.05) * mm, "end": v(525.8, -19.29) * mm});
            skArc(sketch, "E262.MirrorCS", {"start": v(404, 40.6) * mm, "mid": v(405.99, 37.75) * mm, "end": v(409.34, 36.85) * mm});
            skArc(sketch, "E263.MirrorCS", {"start": v(457.33, 4.62) * mm, "mid": v(458.8, 8.66) * mm, "end": v(456.65, 12.38) * mm});
            skPoint(sketch, "E264.endSnap0", {"position": v(0.12, 146.91) * mm});
            skArc(sketch, "E265.MirrorCS", {"start": v(-103.23, 131.73) * mm, "mid": v(-103.51, 135.2) * mm, "end": v(-101.5, 138.03) * mm});
            skLineSegment(sketch, "E266.MirrorCS", {"start": v(-123.09, 119.44) * mm, "end": v(-121.21, 121.3) * mm});
            skLineSegment(sketch, "E267.MirrorCS", {"start": v(-41.44, 140.98) * mm, "end": v(-48.82, 139.05) * mm});
            skLineSegment(sketch, "E268.MirrorCS", {"start": v(-117.6, 87.09) * mm, "end": v(-122.3, 81.1) * mm});
            skLineSegment(sketch, "E269.MirrorCS", {"start": v(-144.16, 25.04) * mm, "end": v(-145.13, 17.9) * mm});
            skArc(sketch, "E270.MirrorCS", {"start": v(-48.82, 139.05) * mm, "mid": v(-53.04, 139.83) * mm, "end": v(-55.16, 143.56) * mm});
            skArc(sketch, "E271.MirrorCS", {"start": v(-122.3, 81.1) * mm, "mid": v(-126.14, 79.16) * mm, "end": v(-130.08, 80.86) * mm});
            skLineSegment(sketch, "E272.MirrorCS", {"start": v(-172.33, -2.42) * mm, "end": v(-172.3, 0.12) * mm});
            skArc(sketch, "E273.MirrorCS", {"start": v(-123.7, 112.94) * mm, "mid": v(-124.58, 116.3) * mm, "end": v(-123.09, 119.44) * mm});
            skLineSegment(sketch, "E274.MirrorCS", {"start": v(-63.08, 132.46) * mm, "end": v(-69.51, 129.2) * mm});
            skArc(sketch, "E275.MirrorCS", {"start": v(-141.75, 39.72) * mm, "mid": v(-144.53, 36.44) * mm, "end": v(-148.82, 36.47) * mm});
            skArc(sketch, "E276.MirrorCS", {"start": v(-138.47, 100.28) * mm, "mid": v(-135.51, 102.11) * mm, "end": v(-132.07, 101.62) * mm});
            skArc(sketch, "E277.MirrorCS", {"start": v(-99.41, 139.47) * mm, "mid": v(-96.05, 140.35) * mm, "end": v(-92.91, 138.86) * mm});
            skArc(sketch, "E278.MirrorCS", {"start": v(-152.63, 77.88) * mm, "mid": v(-149.95, 80.1) * mm, "end": v(-146.47, 80.07) * mm});
            skArc(sketch, "E279.MirrorCS", {"start": v(-144.15, 53.47) * mm, "mid": v(-140.44, 51.3) * mm, "end": v(-139.72, 47.06) * mm});
            skLineSegment(sketch, "E280.MirrorCS", {"start": v(-147.73, 2.5) * mm, "end": v(-147.78, -5.12) * mm});
            skArc(sketch, "E281.MirrorCS", {"start": v(-82.64, 128.45) * mm, "mid": v(-81.2, 124.4) * mm, "end": v(-83.36, 120.7) * mm});
            skArc(sketch, "E282.MirrorCS", {"start": v(-27.5, 145.1) * mm, "mid": v(-31.53, 146.59) * mm, "end": v(-32.97, 150.63) * mm});
            skArc(sketch, "E283.MirrorCS", {"start": v(-107.76, 100.36) * mm, "mid": v(-111.8, 98.92) * mm, "end": v(-115.51, 101.09) * mm});
            skLineSegment(sketch, "E284.MirrorCS", {"start": v(-140.04, 98.29) * mm, "end": v(-138.47, 100.28) * mm});
            skLineSegment(sketch, "E285.MirrorCS", {"start": v(-52.56, 163.46) * mm, "end": v(-50.1, 164.1) * mm});
            skLineSegment(sketch, "E286.MirrorCS", {"start": v(-26.95, 169.78) * mm, "end": v(-24.42, 169.99) * mm});
            skArc(sketch, "E287.MirrorCS", {"start": v(-24.42, 169.99) * mm, "mid": v(-21.07, 169.06) * mm, "end": v(-19.1, 166.2) * mm});
            skArc(sketch, "E288.MirrorCS", {"start": v(-50.1, 164.1) * mm, "mid": v(-46.64, 163.78) * mm, "end": v(-44.2, 161.3) * mm});
            skArc(sketch, "E289.MirrorCS", {"start": v(-102.96, 113.48) * mm, "mid": v(-100.83, 109.75) * mm, "end": v(-102.33, 105.72) * mm});
            skArc(sketch, "E290.MirrorCS", {"start": v(-76.44, 153.22) * mm, "mid": v(-73, 153.64) * mm, "end": v(-70.08, 151.74) * mm});
            skLineSegment(sketch, "E291.MirrorCS", {"start": v(-83.36, 120.7) * mm, "end": v(-89.63, 116.37) * mm});
            skArc(sketch, "E292.MirrorCS", {"start": v(-172.3, 0.12) * mm, "mid": v(-171.1, 3.38) * mm, "end": v(-168.08, 5.1) * mm});
            skArc(sketch, "E293.MirrorCS", {"start": v(-164.08, 51.13) * mm, "mid": v(-162.07, 53.96) * mm, "end": v(-158.71, 54.84) * mm});
            skLineSegment(sketch, "E294.MirrorCS", {"start": v(-164.76, 48.68) * mm, "end": v(-164.08, 51.13) * mm});
            skArc(sketch, "E295.MirrorCS", {"start": v(-162.04, 42.74) * mm, "mid": v(-164.48, 45.21) * mm, "end": v(-164.76, 48.68) * mm});
            skArc(sketch, "E296.MirrorCS", {"start": v(-165.65, 18.23) * mm, "mid": v(-168.4, 20.35) * mm, "end": v(-169.13, 23.75) * mm});
            skLineSegment(sketch, "E297.MirrorCS", {"start": v(-102.33, 105.72) * mm, "end": v(-107.76, 100.36) * mm});
            skArc(sketch, "E298.MirrorCS", {"start": v(-80.92, 146.25) * mm, "mid": v(-80.73, 149.72) * mm, "end": v(-78.35, 152.26) * mm});
            skArc(sketch, "E299.MirrorCS", {"start": v(-119.18, 94.7) * mm, "mid": v(-116.61, 91.27) * mm, "end": v(-117.6, 87.09) * mm});
            skArc(sketch, "E300.MirrorCS", {"start": v(-61.3, 140.04) * mm, "mid": v(-60.43, 135.83) * mm, "end": v(-63.08, 132.46) * mm});
            skLineSegment(sketch, "E301.MirrorCS", {"start": v(-153.9, 75.69) * mm, "end": v(-152.63, 77.88) * mm});
            skArc(sketch, "E302.MirrorCS", {"start": v(-56.34, 158.14) * mm, "mid": v(-55.42, 161.49) * mm, "end": v(-52.56, 163.46) * mm});
            skLineSegment(sketch, "E303.MirrorCS", {"start": v(-169.13, 23.75) * mm, "end": v(-168.84, 25.85) * mm});
            skLineSegment(sketch, "E304.MirrorCS", {"start": v(-139.72, 47.06) * mm, "end": v(-141.75, 39.72) * mm});
            skArc(sketch, "E305.MirrorCS", {"start": v(-89.63, 116.37) * mm, "mid": v(-93.87, 115.65) * mm, "end": v(-97.14, 118.44) * mm});
            skArc(sketch, "E306.MirrorCS", {"start": v(-168.84, 25.85) * mm, "mid": v(-167.22, 28.92) * mm, "end": v(-164, 30.24) * mm});
            skArc(sketch, "E307.MirrorCS", {"start": v(-38.1, 148) * mm, "mid": v(-38.14, 143.71) * mm, "end": v(-41.44, 140.98) * mm});
            skLineSegment(sketch, "E308.MirrorCS", {"start": v(-19.9, 145.7) * mm, "end": v(-27.5, 145.1) * mm});
            skArc(sketch, "E309.MirrorCS", {"start": v(-134, 61.07) * mm, "mid": v(-137.53, 58.63) * mm, "end": v(-141.67, 59.77) * mm});
            skArc(sketch, "E310.MirrorCS", {"start": v(-31.6, 165.2) * mm, "mid": v(-30.1, 168.33) * mm, "end": v(-26.95, 169.78) * mm});
            skLineSegment(sketch, "E311.MirrorCS", {"start": v(-130.15, 67.65) * mm, "end": v(-134, 61.07) * mm});
            skArc(sketch, "E312.MirrorCS", {"start": v(-132.76, 74.98) * mm, "mid": v(-129.75, 71.92) * mm, "end": v(-130.15, 67.65) * mm});
            skArc(sketch, "E313.MirrorCS", {"start": v(-139.83, 91.76) * mm, "mid": v(-141.12, 94.99) * mm, "end": v(-140.04, 98.29) * mm});
            skArc(sketch, "E314.MirrorCS", {"start": v(-145.13, 17.9) * mm, "mid": v(-147.46, 14.3) * mm, "end": v(-151.72, 13.76) * mm});
            skLineSegment(sketch, "E315.MirrorCS", {"start": v(-78.35, 152.26) * mm, "end": v(-76.44, 153.22) * mm});
            skArc(sketch, "E316.MirrorCS", {"start": v(-121.21, 121.3) * mm, "mid": v(-118.05, 122.74) * mm, "end": v(-114.7, 121.82) * mm});
            skArc(sketch, "E317.MirrorCS", {"start": v(-152.82, 69.25) * mm, "mid": v(-154.54, 72.27) * mm, "end": v(-153.9, 75.69) * mm});
            skLineSegment(sketch, "E318.MirrorCS", {"start": v(-101.5, 138.03) * mm, "end": v(-99.41, 139.47) * mm});
            skArc(sketch, "E319.MirrorCS", {"start": v(-168.16, -7.45) * mm, "mid": v(-171.16, -5.7) * mm, "end": v(-172.33, -2.42) * mm});
            skArc(sketch, "E320.MirrorCS", {"start": v(-69.51, 129.2) * mm, "mid": v(-73.8, 129.06) * mm, "end": v(-76.67, 132.25) * mm});
            skArc(sketch, "E321.MirrorCS", {"start": v(-153.66, 7.54) * mm, "mid": v(-149.52, 6.4) * mm, "end": v(-147.73, 2.5) * mm});
            skArc(sketch, "E322.MirrorCS", {"start": v(-149.39, 30.8) * mm, "mid": v(-145.43, 29.14) * mm, "end": v(-144.16, 25.04) * mm});
            skArc(sketch, "E323.MirrorCS", {"start": v(-15.4, 152.05) * mm, "mid": v(-16.17, 147.83) * mm, "end": v(-19.9, 145.7) * mm});
            skLineSegment(sketch, "E324.MirrorCS", {"start": v(-158.71, 54.84) * mm, "end": v(-144.15, 53.47) * mm});
            skLineSegment(sketch, "E325.MirrorCS", {"start": v(-114.7, 121.82) * mm, "end": v(-102.96, 113.48) * mm});
            skLineSegment(sketch, "E326.MirrorCS", {"start": v(-164, 30.24) * mm, "end": v(-149.39, 30.8) * mm});
            skLineSegment(sketch, "E327.MirrorCS", {"start": v(-132.07, 101.62) * mm, "end": v(-119.18, 94.7) * mm});
            skLineSegment(sketch, "E328.MirrorCS", {"start": v(-19.1, 166.2) * mm, "end": v(-15.4, 152.05) * mm});
            skLineSegment(sketch, "E329.MirrorCS", {"start": v(-97.14, 118.44) * mm, "end": v(-103.23, 131.73) * mm});
            skLineSegment(sketch, "E330.MirrorCS", {"start": v(-70.08, 151.74) * mm, "end": v(-61.3, 140.04) * mm});
            skLineSegment(sketch, "E331.MirrorCS", {"start": v(-168.08, 5.1) * mm, "end": v(-153.66, 7.54) * mm});
            skLineSegment(sketch, "E332.MirrorCS", {"start": v(-141.67, 59.77) * mm, "end": v(-152.82, 69.25) * mm});
            skLineSegment(sketch, "E333.MirrorCS", {"start": v(-55.16, 143.56) * mm, "end": v(-56.34, 158.14) * mm});
            skLineSegment(sketch, "E334.MirrorCS", {"start": v(-115.51, 101.09) * mm, "end": v(-123.7, 112.94) * mm});
            skLineSegment(sketch, "E335.MirrorCS", {"start": v(-148.82, 36.47) * mm, "end": v(-162.04, 42.74) * mm});
            skLineSegment(sketch, "E336.MirrorCS", {"start": v(-32.97, 150.63) * mm, "end": v(-31.6, 165.2) * mm});
            skLineSegment(sketch, "E337.MirrorCS", {"start": v(-44.2, 161.3) * mm, "end": v(-38.1, 148) * mm});
            skLineSegment(sketch, "E338.MirrorCS", {"start": v(-92.91, 138.86) * mm, "end": v(-82.64, 128.45) * mm});
            skLineSegment(sketch, "E339.MirrorCS", {"start": v(-151.72, 13.76) * mm, "end": v(-165.65, 18.23) * mm});
            skLineSegment(sketch, "E340.MirrorCS", {"start": v(-146.47, 80.07) * mm, "end": v(-132.76, 74.98) * mm});
            skArc(sketch, "E341.MirrorCS", {"start": v(-147.78, -5.12) * mm, "mid": v(-149.62, -9) * mm, "end": v(-153.77, -10.09) * mm});
            skLineSegment(sketch, "E342.MirrorCS", {"start": v(-153.77, -10.09) * mm, "end": v(-168.16, -7.45) * mm});
            skPoint(sketch, "E343.MirrorP", {"position": v(-15.84, 145.6) * mm});
            skLineSegment(sketch, "E344.MirrorCS", {"start": v(-130.08, 80.86) * mm, "end": v(-139.83, 91.76) * mm});
            skLineSegment(sketch, "E345.MirrorCS", {"start": v(-76.67, 132.25) * mm, "end": v(-80.92, 146.25) * mm});
            skLineSegment(sketch, "E346.MirrorCS", {"start": v(-1.15, -173.5) * mm, "end": v(1.4, -173.5) * mm});
            skLineSegment(sketch, "E347.MirrorCS", {"start": v(3.93, -148.94) * mm, "end": v(-3.69, -148.94) * mm});
            skLineSegment(sketch, "E348.MirrorCS", {"start": v(1.15, -173.5) * mm, "end": v(-1.4, -173.5) * mm});
            skLineSegment(sketch, "E349.MirrorCS", {"start": v(-3.93, -148.94) * mm, "end": v(3.69, -148.94) * mm});
            skArc(sketch, "E350.MirrorCS", {"start": v(-8.94, -154.9) * mm, "mid": v(-7.82, -150.75) * mm, "end": v(-3.93, -148.94) * mm});
            skLineSegment(sketch, "E351.MirrorCS", {"start": v(10.44, -171.31) * mm, "end": v(10.23, -171.22) * mm});
            skLineSegment(sketch, "E352.MirrorCS", {"start": v(-10.44, -171.31) * mm, "end": v(-10.23, -171.22) * mm});
            skArc(sketch, "E353.MirrorCS", {"start": v(8.94, -154.9) * mm, "mid": v(7.82, -150.75) * mm, "end": v(3.93, -148.94) * mm});
            skArc(sketch, "E354.MirrorCS", {"start": v(1.4, -173.5) * mm, "mid": v(4.66, -172.31) * mm, "end": v(6.4, -169.3) * mm});
            skArc(sketch, "E355.MirrorCS", {"start": v(-1.4, -173.5) * mm, "mid": v(-4.66, -172.31) * mm, "end": v(-6.4, -169.3) * mm});
            skLineSegment(sketch, "E356.MirrorCS", {"start": v(170.73, -24.67) * mm, "end": v(170.45, -26.77) * mm});
            skLineSegment(sketch, "E357.MirrorCS", {"start": v(155.85, -76.7) * mm, "end": v(154.58, -78.9) * mm});
            skLineSegment(sketch, "E358.MirrorCS", {"start": v(166.52, -49.62) * mm, "end": v(165.86, -52.07) * mm});
            skArc(sketch, "E359.MirrorCS", {"start": v(-132.76, -77) * mm, "mid": v(-129.75, -73.95) * mm, "end": v(-130.15, -69.67) * mm});
            skLineSegment(sketch, "E360.MirrorCS", {"start": v(-139.72, -49.09) * mm, "end": v(-141.75, -41.74) * mm});
            skLineSegment(sketch, "E361.MirrorCS", {"start": v(-19.9, -147.73) * mm, "end": v(-27.5, -147.12) * mm});
            skArc(sketch, "E362.MirrorCS", {"start": v(154.71, -70.27) * mm, "mid": v(156.45, -73.28) * mm, "end": v(155.85, -76.7) * mm});
            skArc(sketch, "E363.MirrorCS", {"start": v(-138.47, -102.3) * mm, "mid": v(-135.51, -104.14) * mm, "end": v(-132.07, -103.64) * mm});
            skArc(sketch, "E364.MirrorCS", {"start": v(-162.04, -44.76) * mm, "mid": v(-164.48, -47.24) * mm, "end": v(-164.76, -50.7) * mm});
            skLineSegment(sketch, "E365.MirrorCS", {"start": v(80.79, -153.76) * mm, "end": v(78.89, -154.74) * mm});
            skArc(sketch, "E366.MirrorCS", {"start": v(34.12, -167) * mm, "mid": v(32.65, -170.15) * mm, "end": v(29.5, -171.62) * mm});
            skArc(sketch, "E367.MirrorCS", {"start": v(-38.1, -150.03) * mm, "mid": v(-38.14, -145.74) * mm, "end": v(-41.44, -143) * mm});
            skArc(sketch, "E368.MirrorCS", {"start": v(-122.3, -83.12) * mm, "mid": v(-126.14, -81.19) * mm, "end": v(-130.08, -82.88) * mm});
            skArc(sketch, "E369.MirrorCS", {"start": v(-152.82, -71.27) * mm, "mid": v(-154.54, -74.3) * mm, "end": v(-153.9, -77.71) * mm});
            skArc(sketch, "E370.MirrorCS", {"start": v(-61.3, -142.06) * mm, "mid": v(-60.43, -137.86) * mm, "end": v(-63.08, -134.48) * mm});
            skArc(sketch, "E371.MirrorCS", {"start": v(-99.41, -141.5) * mm, "mid": v(-96.05, -142.37) * mm, "end": v(-92.91, -140.89) * mm});
            skArc(sketch, "E372.MirrorCS", {"start": v(-139.83, -93.78) * mm, "mid": v(-141.12, -97.01) * mm, "end": v(-140.04, -100.31) * mm});
            skArc(sketch, "E373.MirrorCS", {"start": v(-31.6, -167.22) * mm, "mid": v(-30.1, -170.36) * mm, "end": v(-26.95, -171.8) * mm});
            skLineSegment(sketch, "E374.MirrorCS", {"start": v(43.8, -142.72) * mm, "end": v(51.17, -140.75) * mm});
            skArc(sketch, "E375.MirrorCS", {"start": v(-15.4, -154.08) * mm, "mid": v(-16.17, -149.85) * mm, "end": v(-19.9, -147.73) * mm});
            skLineSegment(sketch, "E376.MirrorCS", {"start": v(-140.04, -100.31) * mm, "end": v(-138.47, -102.3) * mm});
            skArc(sketch, "E377.MirrorCS", {"start": v(17.84, -153.97) * mm, "mid": v(18.59, -149.74) * mm, "end": v(22.3, -147.6) * mm});
            skArc(sketch, "E378.MirrorCS", {"start": v(143.45, -40.8) * mm, "mid": v(146.2, -37.52) * mm, "end": v(150.5, -37.52) * mm});
            skArc(sketch, "E379.MirrorCS", {"start": v(52.62, -165.8) * mm, "mid": v(49.16, -165.5) * mm, "end": v(46.7, -163.03) * mm});
            skLineSegment(sketch, "E380.MirrorCS", {"start": v(65.39, -134.06) * mm, "end": v(71.8, -130.76) * mm});
            skArc(sketch, "E381.MirrorCS", {"start": v(105.54, -133.08) * mm, "mid": v(105.84, -136.54) * mm, "end": v(103.85, -139.38) * mm});
            skArc(sketch, "E382.MirrorCS", {"start": v(-24.42, -172.01) * mm, "mid": v(-21.07, -171.09) * mm, "end": v(-19.1, -168.23) * mm});
            skArc(sketch, "E383.MirrorCS", {"start": v(154.58, -78.9) * mm, "mid": v(151.92, -81.13) * mm, "end": v(148.44, -81.13) * mm});
            skArc(sketch, "E384.MirrorCS", {"start": v(-102.96, -115.5) * mm, "mid": v(-100.83, -111.77) * mm, "end": v(-102.33, -107.75) * mm});
            skLineSegment(sketch, "E385.MirrorCS", {"start": v(-26.95, -171.8) * mm, "end": v(-24.42, -172.01) * mm});
            skArc(sketch, "E386.MirrorCS", {"start": v(141.88, -92.86) * mm, "mid": v(143.19, -96.08) * mm, "end": v(142.12, -99.4) * mm});
            skLineSegment(sketch, "E387.MirrorCS", {"start": v(22.3, -147.6) * mm, "end": v(29.9, -146.93) * mm});
            skArc(sketch, "E388.MirrorCS", {"start": v(-50.1, -166.13) * mm, "mid": v(-46.64, -165.8) * mm, "end": v(-44.2, -163.33) * mm});
            skLineSegment(sketch, "E389.MirrorCS", {"start": v(-123.09, -121.47) * mm, "end": v(-121.21, -123.32) * mm});
            skArc(sketch, "E390.MirrorCS", {"start": v(-141.75, -41.74) * mm, "mid": v(-144.53, -38.47) * mm, "end": v(-148.82, -38.5) * mm});
            skArc(sketch, "E391.MirrorCS", {"start": v(83.32, -147.74) * mm, "mid": v(83.15, -151.21) * mm, "end": v(80.79, -153.76) * mm});
            skLineSegment(sketch, "E392.MirrorCS", {"start": v(-41.44, -143) * mm, "end": v(-48.82, -141.08) * mm});
            skLineSegment(sketch, "E393.MirrorCS", {"start": v(119.6, -88.34) * mm, "end": v(124.28, -82.32) * mm});
            skLineSegment(sketch, "E394.MirrorCS", {"start": v(-169.13, -25.78) * mm, "end": v(-168.84, -27.87) * mm});
            skLineSegment(sketch, "E395.MirrorCS", {"start": v(-52.56, -165.49) * mm, "end": v(-50.1, -166.13) * mm});
            skArc(sketch, "E396.MirrorCS", {"start": v(-56.34, -160.16) * mm, "mid": v(-55.42, -163.51) * mm, "end": v(-52.56, -165.49) * mm});
            skArc(sketch, "E397.MirrorCS", {"start": v(125.88, -114.15) * mm, "mid": v(126.78, -117.5) * mm, "end": v(125.31, -120.66) * mm});
            skArc(sketch, "E398.MirrorCS", {"start": v(165.86, -52.07) * mm, "mid": v(163.87, -54.92) * mm, "end": v(160.51, -55.82) * mm});
            skLineSegment(sketch, "E399.MirrorCS", {"start": v(145.77, -26.12) * mm, "end": v(146.7, -18.98) * mm});
            skArc(sketch, "E400.MirrorCS", {"start": v(84.92, -129.93) * mm, "mid": v(83.45, -125.9) * mm, "end": v(85.6, -122.17) * mm});
            skLineSegment(sketch, "E401.MirrorCS", {"start": v(-117.6, -89.11) * mm, "end": v(-122.3, -83.12) * mm});
            skLineSegment(sketch, "E402.MirrorCS", {"start": v(142.12, -99.4) * mm, "end": v(140.57, -101.4) * mm});
            skLineSegment(sketch, "E403.MirrorCS", {"start": v(-63.08, -134.48) * mm, "end": v(-69.51, -131.22) * mm});
            skArc(sketch, "E404.MirrorCS", {"start": v(-80.92, -148.28) * mm, "mid": v(-80.73, -151.75) * mm, "end": v(-78.35, -154.28) * mm});
            skArc(sketch, "E405.MirrorCS", {"start": v(109.86, -101.67) * mm, "mid": v(113.9, -100.2) * mm, "end": v(117.62, -102.35) * mm});
            skLineSegment(sketch, "E406.MirrorCS", {"start": v(-78.35, -154.28) * mm, "end": v(-76.44, -155.25) * mm});
            skLineSegment(sketch, "E407.MirrorCS", {"start": v(-130.15, -69.67) * mm, "end": v(-134, -63.1) * mm});
            skLineSegment(sketch, "E408.MirrorCS", {"start": v(-101.5, -140.05) * mm, "end": v(-99.41, -141.5) * mm});
            skArc(sketch, "E409.MirrorCS", {"start": v(-103.23, -133.76) * mm, "mid": v(-103.51, -137.22) * mm, "end": v(-101.5, -140.05) * mm});
            skArc(sketch, "E410.MirrorCS", {"start": v(101.77, -140.84) * mm, "mid": v(98.41, -141.74) * mm, "end": v(95.26, -140.27) * mm});
            skArc(sketch, "E411.MirrorCS", {"start": v(26.98, -171.84) * mm, "mid": v(23.62, -170.94) * mm, "end": v(21.63, -168.1) * mm});
            skArc(sketch, "E412.MirrorCS", {"start": v(123.45, -122.52) * mm, "mid": v(120.3, -123.99) * mm, "end": v(116.94, -123.09) * mm});
            skArc(sketch, "E413.MirrorCS", {"start": v(146.7, -18.98) * mm, "mid": v(149, -15.35) * mm, "end": v(153.25, -14.79) * mm});
            skLineSegment(sketch, "E414.MirrorCS", {"start": v(132.03, -68.82) * mm, "end": v(135.84, -62.22) * mm});
            skArc(sketch, "E415.MirrorCS", {"start": v(-164.08, -53.15) * mm, "mid": v(-162.07, -55.98) * mm, "end": v(-158.71, -56.86) * mm});
            skArc(sketch, "E416.MirrorCS", {"start": v(134.7, -76.13) * mm, "mid": v(131.66, -73.1) * mm, "end": v(132.03, -68.82) * mm});
            skArc(sketch, "E417.MirrorCS", {"start": v(-107.76, -102.38) * mm, "mid": v(-111.8, -100.94) * mm, "end": v(-115.51, -103.11) * mm});
            skArc(sketch, "E418.MirrorCS", {"start": v(105.14, -114.83) * mm, "mid": v(103, -111.1) * mm, "end": v(104.46, -107.07) * mm});
            skArc(sketch, "E419.MirrorCS", {"start": v(163.76, -43.7) * mm, "mid": v(166.22, -46.16) * mm, "end": v(166.52, -49.62) * mm});
            skArc(sketch, "E420.MirrorCS", {"start": v(-134, -63.1) * mm, "mid": v(-137.53, -60.66) * mm, "end": v(-141.67, -61.8) * mm});
            skArc(sketch, "E421.MirrorCS", {"start": v(63.67, -141.65) * mm, "mid": v(62.76, -137.46) * mm, "end": v(65.39, -134.06) * mm});
            skLineSegment(sketch, "E422.MirrorCS", {"start": v(29.5, -171.62) * mm, "end": v(26.98, -171.84) * mm});
            skLineSegment(sketch, "E423.MirrorCS", {"start": v(125.31, -120.66) * mm, "end": v(123.45, -122.52) * mm});
            skArc(sketch, "E424.MirrorCS", {"start": v(78.89, -154.74) * mm, "mid": v(75.44, -155.18) * mm, "end": v(72.52, -153.3) * mm});
            skArc(sketch, "E425.MirrorCS", {"start": v(-119.18, -96.73) * mm, "mid": v(-116.61, -93.3) * mm, "end": v(-117.6, -89.11) * mm});
            skArc(sketch, "E426.MirrorCS", {"start": v(-165.65, -20.25) * mm, "mid": v(-168.4, -22.38) * mm, "end": v(-169.13, -25.78) * mm});
            skArc(sketch, "E427.MirrorCS", {"start": v(135.84, -62.22) * mm, "mid": v(139.36, -59.76) * mm, "end": v(143.5, -60.87) * mm});
            skArc(sketch, "E428.MirrorCS", {"start": v(167.2, -19.16) * mm, "mid": v(169.97, -21.27) * mm, "end": v(170.73, -24.67) * mm});
            skLineSegment(sketch, "E429.MirrorCS", {"start": v(-164.76, -50.7) * mm, "end": v(-164.08, -53.15) * mm});
            skArc(sketch, "E430.MirrorCS", {"start": v(151.03, -31.85) * mm, "mid": v(147.06, -30.2) * mm, "end": v(145.77, -26.12) * mm});
            skArc(sketch, "E431.MirrorCS", {"start": v(124.28, -82.32) * mm, "mid": v(128.1, -80.36) * mm, "end": v(132.05, -82.02) * mm});
            skLineSegment(sketch, "E432.MirrorCS", {"start": v(-153.9, -77.71) * mm, "end": v(-152.63, -79.9) * mm});
            skLineSegment(sketch, "E433.MirrorCS", {"start": v(85.6, -122.17) * mm, "end": v(91.84, -117.8) * mm});
            skArc(sketch, "E434.MirrorCS", {"start": v(-152.63, -79.9) * mm, "mid": v(-149.95, -82.12) * mm, "end": v(-146.47, -82.1) * mm});
            skArc(sketch, "E435.MirrorCS", {"start": v(-76.44, -155.25) * mm, "mid": v(-73, -155.66) * mm, "end": v(-70.08, -153.76) * mm});
            skArc(sketch, "E436.MirrorCS", {"start": v(121.25, -95.95) * mm, "mid": v(118.65, -92.52) * mm, "end": v(119.6, -88.34) * mm});
            skArc(sketch, "E437.MirrorCS", {"start": v(51.17, -140.75) * mm, "mid": v(55.4, -141.5) * mm, "end": v(57.54, -145.21) * mm});
            skArc(sketch, "E438.MirrorCS", {"start": v(71.8, -130.76) * mm, "mid": v(76.1, -130.6) * mm, "end": v(78.98, -133.77) * mm});
            skLineSegment(sketch, "E439.MirrorCS", {"start": v(103.85, -139.38) * mm, "end": v(101.77, -140.84) * mm});
            skLineSegment(sketch, "E440.MirrorCS", {"start": v(-144.16, -27.06) * mm, "end": v(-145.13, -19.93) * mm});
            skArc(sketch, "E441.MirrorCS", {"start": v(170.45, -26.77) * mm, "mid": v(168.85, -29.85) * mm, "end": v(165.65, -31.19) * mm});
            skLineSegment(sketch, "E442.MirrorCS", {"start": v(141.48, -48.17) * mm, "end": v(143.45, -40.8) * mm});
            skArc(sketch, "E443.MirrorCS", {"start": v(-121.21, -123.32) * mm, "mid": v(-118.05, -124.77) * mm, "end": v(-114.7, -123.85) * mm});
            skArc(sketch, "E444.MirrorCS", {"start": v(-168.84, -27.87) * mm, "mid": v(-167.22, -30.95) * mm, "end": v(-164, -32.26) * mm});
            skArc(sketch, "E445.MirrorCS", {"start": v(58.82, -159.79) * mm, "mid": v(57.92, -163.14) * mm, "end": v(55.07, -165.14) * mm});
            skLineSegment(sketch, "E446.MirrorCS", {"start": v(55.07, -165.14) * mm, "end": v(52.62, -165.8) * mm});
            skArc(sketch, "E447.MirrorCS", {"start": v(-149.39, -32.83) * mm, "mid": v(-145.43, -31.16) * mm, "end": v(-144.16, -27.06) * mm});
            skArc(sketch, "E448.MirrorCS", {"start": v(-89.63, -118.4) * mm, "mid": v(-93.87, -117.68) * mm, "end": v(-97.14, -120.46) * mm});
            skArc(sketch, "E449.MirrorCS", {"start": v(140.57, -101.4) * mm, "mid": v(137.62, -103.25) * mm, "end": v(134.18, -102.77) * mm});
            skArc(sketch, "E450.MirrorCS", {"start": v(-82.64, -130.48) * mm, "mid": v(-81.2, -126.43) * mm, "end": v(-83.36, -122.73) * mm});
            skLineSegment(sketch, "E451.MirrorCS", {"start": v(-83.36, -122.73) * mm, "end": v(-89.63, -118.4) * mm});
            skArc(sketch, "E452.MirrorCS", {"start": v(91.84, -117.8) * mm, "mid": v(96.07, -117.06) * mm, "end": v(99.36, -119.82) * mm});
            skArc(sketch, "E453.MirrorCS", {"start": v(-123.7, -114.97) * mm, "mid": v(-124.58, -118.33) * mm, "end": v(-123.09, -121.47) * mm});
            skLineSegment(sketch, "E454.MirrorCS", {"start": v(-102.33, -107.75) * mm, "end": v(-107.76, -102.38) * mm});
            skLineSegment(sketch, "E455.MirrorCS", {"start": v(104.46, -107.07) * mm, "end": v(109.86, -101.67) * mm});
            skPoint(sketch, "E456.MirrorP", {"position": v(5.4, -173.5) * mm});
            skPoint(sketch, "E457.MirrorP", {"position": v(-9.99, -148.94) * mm});
            skArc(sketch, "E458.MirrorCS", {"start": v(145.94, -54.54) * mm, "mid": v(142.22, -52.4) * mm, "end": v(141.48, -48.17) * mm});
            skPoint(sketch, "E459.MirrorP", {"position": v(-9.74, -148.94) * mm});
            skLineSegment(sketch, "E460.MirrorCS", {"start": v(6.4, -169.3) * mm, "end": v(8.94, -154.9) * mm});
            skArc(sketch, "E461.MirrorCS", {"start": v(40.52, -149.78) * mm, "mid": v(40.52, -145.48) * mm, "end": v(43.8, -142.72) * mm});
            skLineSegment(sketch, "E462.MirrorCS", {"start": v(-115.51, -103.11) * mm, "end": v(-123.7, -114.97) * mm});
            skPoint(sketch, "E463.MirrorP", {"position": v(-15.84, -147.62) * mm});
            skLineSegment(sketch, "E464.MirrorCS", {"start": v(-19.1, -168.23) * mm, "end": v(-15.4, -154.08) * mm});
            skPoint(sketch, "E465.MirrorP", {"position": v(9.74, -148.94) * mm});
            skLineSegment(sketch, "E466.MirrorCS", {"start": v(-158.71, -56.86) * mm, "end": v(-144.15, -55.5) * mm});
            skLineSegment(sketch, "E467.MirrorCS", {"start": v(-151.72, -15.78) * mm, "end": v(-165.65, -20.25) * mm});
            skLineSegment(sketch, "E468.MirrorCS", {"start": v(-148.82, -38.5) * mm, "end": v(-162.04, -44.76) * mm});
            skLineSegment(sketch, "E469.MirrorCS", {"start": v(-130.08, -82.88) * mm, "end": v(-139.83, -93.78) * mm});
            skArc(sketch, "E470.MirrorCS", {"start": v(-48.82, -141.08) * mm, "mid": v(-53.04, -141.85) * mm, "end": v(-55.16, -145.58) * mm});
            skPoint(sketch, "E471.MirrorP", {"position": v(9.99, -148.94) * mm});
            skLineSegment(sketch, "E472.MirrorCS", {"start": v(99.36, -119.82) * mm, "end": v(105.54, -133.08) * mm});
            skLineSegment(sketch, "E473.MirrorCS", {"start": v(160.51, -55.82) * mm, "end": v(145.94, -54.54) * mm});
            skLineSegment(sketch, "E474.MirrorCS", {"start": v(143.5, -60.87) * mm, "end": v(154.71, -70.27) * mm});
            skLineSegment(sketch, "E475.MirrorCS", {"start": v(-97.14, -120.46) * mm, "end": v(-103.23, -133.76) * mm});
            skLineSegment(sketch, "E476.MirrorCS", {"start": v(-132.07, -103.64) * mm, "end": v(-119.18, -96.73) * mm});
            skLineSegment(sketch, "E477.MirrorCS", {"start": v(72.52, -153.3) * mm, "end": v(63.67, -141.65) * mm});
            skLineSegment(sketch, "E478.MirrorCS", {"start": v(-164, -32.26) * mm, "end": v(-149.39, -32.83) * mm});
            skLineSegment(sketch, "E479.MirrorCS", {"start": v(150.5, -37.52) * mm, "end": v(163.76, -43.7) * mm});
            skLineSegment(sketch, "E480.MirrorCS", {"start": v(46.7, -163.03) * mm, "end": v(40.52, -149.78) * mm});
            skLineSegment(sketch, "E481.MirrorCS", {"start": v(-6.4, -169.3) * mm, "end": v(-8.94, -154.9) * mm});
            skLineSegment(sketch, "E482.MirrorCS", {"start": v(-55.16, -145.58) * mm, "end": v(-56.34, -160.16) * mm});
            skLineSegment(sketch, "E483.MirrorCS", {"start": v(165.65, -31.19) * mm, "end": v(151.03, -31.85) * mm});
            skArc(sketch, "E484.MirrorCS", {"start": v(29.9, -146.93) * mm, "mid": v(33.93, -148.4) * mm, "end": v(35.4, -152.43) * mm});
            skLineSegment(sketch, "E485.MirrorCS", {"start": v(57.54, -145.21) * mm, "end": v(58.82, -159.79) * mm});
            skLineSegment(sketch, "E486.MirrorCS", {"start": v(-70.08, -153.76) * mm, "end": v(-61.3, -142.06) * mm});
            skArc(sketch, "E487.MirrorCS", {"start": v(-69.51, -131.22) * mm, "mid": v(-73.8, -131.08) * mm, "end": v(-76.67, -134.28) * mm});
            skLineSegment(sketch, "E488.MirrorCS", {"start": v(117.62, -102.35) * mm, "end": v(125.88, -114.15) * mm});
            skLineSegment(sketch, "E489.MirrorCS", {"start": v(-44.2, -163.33) * mm, "end": v(-38.1, -150.03) * mm});
            skLineSegment(sketch, "E490.MirrorCS", {"start": v(-114.7, -123.85) * mm, "end": v(-102.96, -115.5) * mm});
            skArc(sketch, "E491.MirrorCS", {"start": v(-144.15, -55.5) * mm, "mid": v(-140.44, -53.32) * mm, "end": v(-139.72, -49.09) * mm});
            skPoint(sketch, "E492.MirrorP", {"position": v(18.24, -147.51) * mm});
            skPoint(sketch, "E493.MirrorP", {"position": v(5.66, -173.5) * mm});
            skLineSegment(sketch, "E494.MirrorCS", {"start": v(21.63, -168.1) * mm, "end": v(17.84, -153.97) * mm});
            skLineSegment(sketch, "E495.MirrorCS", {"start": v(134.18, -102.77) * mm, "end": v(121.25, -95.95) * mm});
            skLineSegment(sketch, "E496.MirrorCS", {"start": v(-32.97, -152.65) * mm, "end": v(-31.6, -167.22) * mm});
            skLineSegment(sketch, "E497.MirrorCS", {"start": v(78.98, -133.77) * mm, "end": v(83.32, -147.74) * mm});
            skLineSegment(sketch, "E498.MirrorCS", {"start": v(-92.91, -140.89) * mm, "end": v(-82.64, -130.48) * mm});
            skPoint(sketch, "E499.MirrorP", {"position": v(-5.66, -173.5) * mm});
            skLineSegment(sketch, "E500.MirrorCS", {"start": v(153.25, -14.79) * mm, "end": v(167.2, -19.16) * mm});
            skLineSegment(sketch, "E501.MirrorCS", {"start": v(-76.67, -134.28) * mm, "end": v(-80.92, -148.28) * mm});
            skLineSegment(sketch, "E502.MirrorCS", {"start": v(132.05, -82.02) * mm, "end": v(141.88, -92.86) * mm});
            skPoint(sketch, "E503.MirrorP", {"position": v(0.12, -148.94) * mm});
            skArc(sketch, "E504.MirrorCS", {"start": v(-27.5, -147.12) * mm, "mid": v(-31.53, -148.61) * mm, "end": v(-32.97, -152.65) * mm});
            skLineSegment(sketch, "E505.MirrorCS", {"start": v(-141.67, -61.8) * mm, "end": v(-152.82, -71.27) * mm});
            skLineSegment(sketch, "E506.MirrorCS", {"start": v(116.94, -123.09) * mm, "end": v(105.14, -114.83) * mm});
            skPoint(sketch, "E507.MirrorP", {"position": v(-5.4, -173.5) * mm});
            skLineSegment(sketch, "E508.MirrorCS", {"start": v(148.44, -81.13) * mm, "end": v(134.7, -76.13) * mm});
            skLineSegment(sketch, "E509.MirrorCS", {"start": v(-146.47, -82.1) * mm, "end": v(-132.76, -77) * mm});
            skLineSegment(sketch, "E510.MirrorCS", {"start": v(35.4, -152.43) * mm, "end": v(34.12, -167) * mm});
            skLineSegment(sketch, "E511.MirrorCS", {"start": v(95.26, -140.27) * mm, "end": v(84.92, -129.93) * mm});
            skArc(sketch, "E512.MirrorCS", {"start": v(-145.13, -19.93) * mm, "mid": v(-147.46, -16.32) * mm, "end": v(-151.72, -15.78) * mm});
            skCircle(sketch, "E513", {"center": v(-255.46, 65.3) * mm, "radius": 76.2 * mm});
            skCircle(sketch, "E514", {"center": v(-255.46, 65.3) * mm, "radius": 6.35 * mm});
            skLineSegment(sketch, "E515", {"start": v(-259.83, 136.94) * mm, "end": v(-252.2, 136.94) * mm});
            skLineSegment(sketch, "E516", {"start": v(-247.2, 142.9) * mm, "end": v(-249.74, 157.3) * mm});
            skLineSegment(sketch, "E517", {"start": v(-254.75, 161.5) * mm, "end": v(-257.29, 161.5) * mm});
            skLineSegment(sketch, "E518", {"start": v(-262.29, 157.3) * mm, "end": v(-264.83, 142.9) * mm});
            skArc(sketch, "E519.filletArc", {"start": v(-249.74, 157.3) * mm, "mid": v(-251.48, 160.31) * mm, "end": v(-254.75, 161.5) * mm});
            skArc(sketch, "E520.filletArc", {"start": v(-257.29, 161.5) * mm, "mid": v(-260.55, 160.31) * mm, "end": v(-262.29, 157.3) * mm});
            skArc(sketch, "E521.filletArc", {"start": v(-264.83, 142.9) * mm, "mid": v(-263.72, 138.75) * mm, "end": v(-259.83, 136.94) * mm});
            skArc(sketch, "E522.filletArc", {"start": v(-252.2, 136.94) * mm, "mid": v(-248.31, 138.75) * mm, "end": v(-247.2, 142.9) * mm});
            skLineSegment(sketch, "E523", {"start": v(-237.39, 134.56) * mm, "end": v(-230.23, 131.96) * mm});
            skLineSegment(sketch, "E524", {"start": v(-223.49, 135.85) * mm, "end": v(-220.95, 150.26) * mm});
            skLineSegment(sketch, "E525", {"start": v(-224.21, 155.91) * mm, "end": v(-226.6, 156.78) * mm});
            skLineSegment(sketch, "E526", {"start": v(-232.74, 154.55) * mm, "end": v(-240.05, 141.88) * mm});
            skArc(sketch, "E527.filletArc", {"start": v(-220.95, 150.26) * mm, "mid": v(-221.55, 153.68) * mm, "end": v(-224.21, 155.91) * mm});
            skArc(sketch, "E528.filletArc", {"start": v(-226.6, 156.78) * mm, "mid": v(-230.07, 156.78) * mm, "end": v(-232.74, 154.55) * mm});
            skArc(sketch, "E529.filletArc", {"start": v(-240.05, 141.88) * mm, "mid": v(-240.42, 137.6) * mm, "end": v(-237.39, 134.56) * mm});
            skArc(sketch, "E530.filletArc", {"start": v(-230.23, 131.96) * mm, "mid": v(-225.95, 132.33) * mm, "end": v(-223.49, 135.85) * mm});
            skLineSegment(sketch, "E531", {"start": v(-217.57, 124.25) * mm, "end": v(-211.33, 119.88) * mm});
            skLineSegment(sketch, "E532", {"start": v(-203.81, 121.9) * mm, "end": v(-197.63, 135.15) * mm});
            skLineSegment(sketch, "E533", {"start": v(-199.32, 141.46) * mm, "end": v(-201.4, 142.92) * mm});
            skLineSegment(sketch, "E534", {"start": v(-207.9, 142.35) * mm, "end": v(-218.25, 132) * mm});
            skArc(sketch, "E535.filletArc", {"start": v(-197.63, 135.15) * mm, "mid": v(-197.33, 138.61) * mm, "end": v(-199.32, 141.46) * mm});
            skArc(sketch, "E536.filletArc", {"start": v(-201.4, 142.92) * mm, "mid": v(-204.76, 143.82) * mm, "end": v(-207.9, 142.35) * mm});
            skArc(sketch, "E537.filletArc", {"start": v(-218.25, 132) * mm, "mid": v(-219.72, 127.97) * mm, "end": v(-217.57, 124.25) * mm});
            skArc(sketch, "E538.filletArc", {"start": v(-211.33, 119.88) * mm, "mid": v(-207.1, 119.13) * mm, "end": v(-203.81, 121.9) * mm});
            skLineSegment(sketch, "E539", {"start": v(-200.98, 110.1) * mm, "end": v(-196.6, 103.86) * mm});
            skLineSegment(sketch, "E540", {"start": v(-188.85, 103.19) * mm, "end": v(-178.5, 113.53) * mm});
            skLineSegment(sketch, "E541", {"start": v(-177.94, 120.03) * mm, "end": v(-179.4, 122.12) * mm});
            skLineSegment(sketch, "E542", {"start": v(-185.7, 123.8) * mm, "end": v(-198.96, 117.62) * mm});
            skArc(sketch, "E543.filletArc", {"start": v(-178.5, 113.53) * mm, "mid": v(-177.04, 116.68) * mm, "end": v(-177.94, 120.03) * mm});
            skArc(sketch, "E544.filletArc", {"start": v(-179.4, 122.12) * mm, "mid": v(-182.24, 124.1) * mm, "end": v(-185.7, 123.8) * mm});
            skArc(sketch, "E545.filletArc", {"start": v(-198.96, 117.62) * mm, "mid": v(-201.72, 114.33) * mm, "end": v(-200.98, 110.1) * mm});
            skArc(sketch, "E546.filletArc", {"start": v(-196.6, 103.86) * mm, "mid": v(-192.89, 101.72) * mm, "end": v(-188.85, 103.19) * mm});
            skLineSegment(sketch, "E547", {"start": v(-189.3, 92.12) * mm, "end": v(-187.33, 84.76) * mm});
            skLineSegment(sketch, "E548", {"start": v(-180.28, 81.47) * mm, "end": v(-167.02, 87.66) * mm});
            skLineSegment(sketch, "E549", {"start": v(-164.26, 93.57) * mm, "end": v(-164.92, 96.03) * mm});
            skLineSegment(sketch, "E550", {"start": v(-170.27, 99.77) * mm, "end": v(-184.84, 98.5) * mm});
            skArc(sketch, "E551.filletArc", {"start": v(-167.02, 87.66) * mm, "mid": v(-164.56, 90.11) * mm, "end": v(-164.26, 93.57) * mm});
            skArc(sketch, "E552.filletArc", {"start": v(-164.92, 96.03) * mm, "mid": v(-166.91, 98.87) * mm, "end": v(-170.27, 99.77) * mm});
            skArc(sketch, "E553.filletArc", {"start": v(-184.84, 98.5) * mm, "mid": v(-188.56, 96.35) * mm, "end": v(-189.3, 92.12) * mm});
            skArc(sketch, "E554.filletArc", {"start": v(-187.33, 84.76) * mm, "mid": v(-184.57, 81.47) * mm, "end": v(-180.28, 81.47) * mm});
            skLineSegment(sketch, "E555", {"start": v(-181.68, 70.12) * mm, "end": v(-181.57, 62.5) * mm});
            skLineSegment(sketch, "E556", {"start": v(-175.53, 57.58) * mm, "end": v(-161.17, 60.33) * mm});
            skLineSegment(sketch, "E557", {"start": v(-157.04, 65.4) * mm, "end": v(-157.08, 67.93) * mm});
            skLineSegment(sketch, "E558", {"start": v(-161.35, 72.87) * mm, "end": v(-175.78, 75.2) * mm});
            skArc(sketch, "E559.filletArc", {"start": v(-161.17, 60.33) * mm, "mid": v(-158.18, 62.1) * mm, "end": v(-157.04, 65.4) * mm});
            skArc(sketch, "E560.filletArc", {"start": v(-157.08, 67.93) * mm, "mid": v(-158.31, 71.18) * mm, "end": v(-161.35, 72.87) * mm});
            skArc(sketch, "E561.filletArc", {"start": v(-175.78, 75.2) * mm, "mid": v(-179.92, 74.04) * mm, "end": v(-181.68, 70.12) * mm});
            skArc(sketch, "E562.filletArc", {"start": v(-181.57, 62.5) * mm, "mid": v(-179.7, 58.64) * mm, "end": v(-175.53, 57.58) * mm});
            skLineSegment(sketch, "E563.MirrorCS", {"start": v(-353.89, 65.4) * mm, "end": v(-353.85, 67.93) * mm});
            skLineSegment(sketch, "E564.MirrorCS", {"start": v(-346.67, 93.57) * mm, "end": v(-346.01, 96.03) * mm});
            skArc(sketch, "E565.MirrorCS", {"start": v(-353.85, 67.93) * mm, "mid": v(-352.62, 71.18) * mm, "end": v(-349.58, 72.87) * mm});
            skArc(sketch, "E566.MirrorCS", {"start": v(-331.53, 122.12) * mm, "mid": v(-328.69, 124.1) * mm, "end": v(-325.22, 123.8) * mm});
            skArc(sketch, "E567.MirrorCS", {"start": v(-335.14, 75.2) * mm, "mid": v(-331.01, 74.04) * mm, "end": v(-329.25, 70.12) * mm});
            skArc(sketch, "E568.MirrorCS", {"start": v(-311.97, 117.62) * mm, "mid": v(-309.2, 114.33) * mm, "end": v(-309.95, 110.1) * mm});
            skArc(sketch, "E569.MirrorCS", {"start": v(-314.32, 103.86) * mm, "mid": v(-318.04, 101.72) * mm, "end": v(-322.08, 103.19) * mm});
            skLineSegment(sketch, "E570.MirrorCS", {"start": v(-293.36, 124.25) * mm, "end": v(-299.6, 119.88) * mm});
            skLineSegment(sketch, "E571.MirrorCS", {"start": v(-321.63, 92.12) * mm, "end": v(-323.6, 84.76) * mm});
            skLineSegment(sketch, "E572.MirrorCS", {"start": v(-311.6, 141.46) * mm, "end": v(-309.53, 142.92) * mm});
            skArc(sketch, "E573.MirrorCS", {"start": v(-343.9, 87.66) * mm, "mid": v(-346.37, 90.11) * mm, "end": v(-346.67, 93.57) * mm});
            skArc(sketch, "E574.MirrorCS", {"start": v(-313.3, 135.15) * mm, "mid": v(-313.6, 138.61) * mm, "end": v(-311.6, 141.46) * mm});
            skArc(sketch, "E575.MirrorCS", {"start": v(-346.01, 96.03) * mm, "mid": v(-344.02, 98.87) * mm, "end": v(-340.66, 99.77) * mm});
            skArc(sketch, "E576.MirrorCS", {"start": v(-309.53, 142.92) * mm, "mid": v(-306.17, 143.82) * mm, "end": v(-303.02, 142.35) * mm});
            skArc(sketch, "E577.MirrorCS", {"start": v(-292.68, 132) * mm, "mid": v(-291.2, 127.97) * mm, "end": v(-293.36, 124.25) * mm});
            skArc(sketch, "E578.MirrorCS", {"start": v(-326.09, 98.5) * mm, "mid": v(-322.37, 96.35) * mm, "end": v(-321.63, 92.12) * mm});
            skArc(sketch, "E579.MirrorCS", {"start": v(-299.6, 119.88) * mm, "mid": v(-303.83, 119.13) * mm, "end": v(-307.12, 121.9) * mm});
            skArc(sketch, "E580.MirrorCS", {"start": v(-323.6, 84.76) * mm, "mid": v(-326.36, 81.47) * mm, "end": v(-330.65, 81.47) * mm});
            skLineSegment(sketch, "E581.MirrorCS", {"start": v(-309.95, 110.1) * mm, "end": v(-314.32, 103.86) * mm});
            skLineSegment(sketch, "E582.MirrorCS", {"start": v(-329.25, 70.12) * mm, "end": v(-329.36, 62.5) * mm});
            skLineSegment(sketch, "E583.MirrorCS", {"start": v(-332.99, 120.03) * mm, "end": v(-331.53, 122.12) * mm});
            skArc(sketch, "E584.MirrorCS", {"start": v(-332.42, 113.53) * mm, "mid": v(-333.89, 116.68) * mm, "end": v(-332.99, 120.03) * mm});
            skArc(sketch, "E585.MirrorCS", {"start": v(-349.76, 60.33) * mm, "mid": v(-352.75, 62.1) * mm, "end": v(-353.89, 65.4) * mm});
            skLineSegment(sketch, "E586.MirrorCS", {"start": v(-325.22, 123.8) * mm, "end": v(-311.97, 117.62) * mm});
            skLineSegment(sketch, "E587.MirrorCS", {"start": v(-349.58, 72.87) * mm, "end": v(-335.14, 75.2) * mm});
            skArc(sketch, "E588.MirrorCS", {"start": v(-329.36, 62.5) * mm, "mid": v(-331.23, 58.64) * mm, "end": v(-335.4, 57.58) * mm});
            skLineSegment(sketch, "E589.MirrorCS", {"start": v(-330.65, 81.47) * mm, "end": v(-343.9, 87.66) * mm});
            skLineSegment(sketch, "E590.MirrorCS", {"start": v(-307.12, 121.9) * mm, "end": v(-313.3, 135.15) * mm});
            skLineSegment(sketch, "E591.MirrorCS", {"start": v(-340.66, 99.77) * mm, "end": v(-326.09, 98.5) * mm});
            skLineSegment(sketch, "E592.MirrorCS", {"start": v(-303.02, 142.35) * mm, "end": v(-292.68, 132) * mm});
            skLineSegment(sketch, "E593.MirrorCS", {"start": v(-322.08, 103.19) * mm, "end": v(-332.42, 113.53) * mm});
            skLineSegment(sketch, "E594.MirrorCS", {"start": v(-335.4, 57.58) * mm, "end": v(-349.76, 60.33) * mm});
            skLineSegment(sketch, "E595", {"start": v(-280.18, 131.4) * mm, "end": v(-273.28, 134.62) * mm});
            skLineSegment(sketch, "E596", {"start": v(-271.26, 142.14) * mm, "end": v(-279.65, 154.12) * mm});
            skLineSegment(sketch, "E597", {"start": v(-285.96, 155.81) * mm, "end": v(-288.26, 154.74) * mm});
            skLineSegment(sketch, "E598", {"start": v(-291.02, 148.82) * mm, "end": v(-287.24, 134.7) * mm});
            skArc(sketch, "E599.filletArc", {"start": v(-279.65, 154.12) * mm, "mid": v(-282.5, 156.12) * mm, "end": v(-285.96, 155.81) * mm});
            skArc(sketch, "E600.filletArc", {"start": v(-288.26, 154.74) * mm, "mid": v(-290.72, 152.28) * mm, "end": v(-291.02, 148.82) * mm});
            skArc(sketch, "E601.filletArc", {"start": v(-287.24, 134.7) * mm, "mid": v(-284.48, 131.4) * mm, "end": v(-280.18, 131.4) * mm});
            skArc(sketch, "E602.filletArc", {"start": v(-273.28, 134.62) * mm, "mid": v(-270.52, 137.91) * mm, "end": v(-271.26, 142.14) * mm});
            skLineSegment(sketch, "E603.MirrorCS", {"start": v(-346.67, 37.03) * mm, "end": v(-346.01, 34.58) * mm});
            skLineSegment(sketch, "E604.MirrorCS", {"start": v(-164.26, 37.03) * mm, "end": v(-164.92, 34.58) * mm});
            skLineSegment(sketch, "E605.MirrorCS", {"start": v(-199.32, -10.85) * mm, "end": v(-201.4, -12.31) * mm});
            skLineSegment(sketch, "E606.MirrorCS", {"start": v(-254.75, -30.9) * mm, "end": v(-257.29, -30.9) * mm});
            skLineSegment(sketch, "E607.MirrorCS", {"start": v(-285.96, -25.2) * mm, "end": v(-288.26, -24.13) * mm});
            skLineSegment(sketch, "E608.MirrorCS", {"start": v(-332.99, 10.57) * mm, "end": v(-331.53, 8.49) * mm});
            skLineSegment(sketch, "E609.MirrorCS", {"start": v(-311.6, -10.85) * mm, "end": v(-309.53, -12.31) * mm});
            skLineSegment(sketch, "E610.MirrorCS", {"start": v(-177.94, 10.57) * mm, "end": v(-179.4, 8.49) * mm});
            skLineSegment(sketch, "E611.MirrorCS", {"start": v(-224.21, -25.3) * mm, "end": v(-226.6, -26.18) * mm});
            skArc(sketch, "E612.MirrorCS", {"start": v(-167.02, 42.95) * mm, "mid": v(-164.56, 40.5) * mm, "end": v(-164.26, 37.03) * mm});
            skArc(sketch, "E613.MirrorCS", {"start": v(-178.5, 17.08) * mm, "mid": v(-177.04, 13.93) * mm, "end": v(-177.94, 10.57) * mm});
            skArc(sketch, "E614.MirrorCS", {"start": v(-230.23, -1.35) * mm, "mid": v(-225.95, -1.73) * mm, "end": v(-223.49, -5.25) * mm});
            skArc(sketch, "E615.MirrorCS", {"start": v(-326.09, 32.1) * mm, "mid": v(-322.37, 34.25) * mm, "end": v(-321.63, 38.48) * mm});
            skArc(sketch, "E616.MirrorCS", {"start": v(-196.6, 26.74) * mm, "mid": v(-192.89, 28.89) * mm, "end": v(-188.85, 27.42) * mm});
            skLineSegment(sketch, "E617.MirrorCS", {"start": v(-189.3, 38.48) * mm, "end": v(-187.33, 45.84) * mm});
            skLineSegment(sketch, "E618.MirrorCS", {"start": v(-217.57, 6.35) * mm, "end": v(-211.33, 10.73) * mm});
            skLineSegment(sketch, "E619.MirrorCS", {"start": v(-259.83, -6.33) * mm, "end": v(-252.2, -6.33) * mm});
            skArc(sketch, "E620.MirrorCS", {"start": v(-299.6, 10.73) * mm, "mid": v(-303.83, 11.47) * mm, "end": v(-307.12, 8.71) * mm});
            skLineSegment(sketch, "E621.MirrorCS", {"start": v(-280.18, -0.8) * mm, "end": v(-273.28, -4.02) * mm});
            skLineSegment(sketch, "E622.MirrorCS", {"start": v(-180.28, 49.13) * mm, "end": v(-167.02, 42.95) * mm});
            skLineSegment(sketch, "E623.MirrorCS", {"start": v(-203.81, 8.71) * mm, "end": v(-197.63, -4.55) * mm});
            skLineSegment(sketch, "E624.MirrorCS", {"start": v(-247.2, -12.3) * mm, "end": v(-249.74, -26.7) * mm});
            skLineSegment(sketch, "E625.MirrorCS", {"start": v(-271.26, -11.54) * mm, "end": v(-279.65, -23.52) * mm});
            skArc(sketch, "E626.MirrorCS", {"start": v(-323.6, 45.84) * mm, "mid": v(-326.36, 49.13) * mm, "end": v(-330.65, 49.13) * mm});
            skLineSegment(sketch, "E627.MirrorCS", {"start": v(-309.95, 20.5) * mm, "end": v(-314.32, 26.74) * mm});
            skArc(sketch, "E628.MirrorCS", {"start": v(-331.53, 8.49) * mm, "mid": v(-328.69, 6.5) * mm, "end": v(-325.22, 6.8) * mm});
            skLineSegment(sketch, "E629.MirrorCS", {"start": v(-170.27, 30.83) * mm, "end": v(-184.84, 32.1) * mm});
            skLineSegment(sketch, "E630.MirrorCS", {"start": v(-207.9, -11.74) * mm, "end": v(-218.25, -1.4) * mm});
            skLineSegment(sketch, "E631.MirrorCS", {"start": v(-262.29, -26.7) * mm, "end": v(-264.83, -12.3) * mm});
            skLineSegment(sketch, "E632.MirrorCS", {"start": v(-291.02, -18.22) * mm, "end": v(-287.24, -4.09) * mm});
            skArc(sketch, "E633.MirrorCS", {"start": v(-279.65, -23.52) * mm, "mid": v(-282.5, -25.51) * mm, "end": v(-285.96, -25.2) * mm});
            skArc(sketch, "E634.MirrorCS", {"start": v(-197.63, -4.55) * mm, "mid": v(-197.33, -8) * mm, "end": v(-199.32, -10.85) * mm});
            skArc(sketch, "E635.MirrorCS", {"start": v(-249.74, -26.7) * mm, "mid": v(-251.48, -29.7) * mm, "end": v(-254.75, -30.9) * mm});
            skArc(sketch, "E636.MirrorCS", {"start": v(-288.26, -24.13) * mm, "mid": v(-290.72, -21.68) * mm, "end": v(-291.02, -18.22) * mm});
            skArc(sketch, "E637.MirrorCS", {"start": v(-332.42, 17.08) * mm, "mid": v(-333.89, 13.93) * mm, "end": v(-332.99, 10.57) * mm});
            skArc(sketch, "E638.MirrorCS", {"start": v(-311.97, 12.98) * mm, "mid": v(-309.2, 16.27) * mm, "end": v(-309.95, 20.5) * mm});
            skArc(sketch, "E639.MirrorCS", {"start": v(-164.92, 34.58) * mm, "mid": v(-166.91, 31.73) * mm, "end": v(-170.27, 30.83) * mm});
            skArc(sketch, "E640.MirrorCS", {"start": v(-201.4, -12.31) * mm, "mid": v(-204.76, -13.21) * mm, "end": v(-207.9, -11.74) * mm});
            skArc(sketch, "E641.MirrorCS", {"start": v(-257.29, -30.9) * mm, "mid": v(-260.55, -29.7) * mm, "end": v(-262.29, -26.7) * mm});
            skArc(sketch, "E642.MirrorCS", {"start": v(-218.25, -1.4) * mm, "mid": v(-219.72, 2.64) * mm, "end": v(-217.57, 6.35) * mm});
            skArc(sketch, "E643.MirrorCS", {"start": v(-264.83, -12.3) * mm, "mid": v(-263.72, -8.15) * mm, "end": v(-259.83, -6.33) * mm});
            skArc(sketch, "E644.MirrorCS", {"start": v(-314.32, 26.74) * mm, "mid": v(-318.04, 28.89) * mm, "end": v(-322.08, 27.42) * mm});
            skArc(sketch, "E645.MirrorCS", {"start": v(-287.24, -4.09) * mm, "mid": v(-284.48, -0.8) * mm, "end": v(-280.18, -0.8) * mm});
            skArc(sketch, "E646.MirrorCS", {"start": v(-184.84, 32.1) * mm, "mid": v(-188.56, 34.25) * mm, "end": v(-189.3, 38.48) * mm});
            skArc(sketch, "E647.MirrorCS", {"start": v(-211.33, 10.73) * mm, "mid": v(-207.1, 11.47) * mm, "end": v(-203.81, 8.71) * mm});
            skArc(sketch, "E648.MirrorCS", {"start": v(-252.2, -6.33) * mm, "mid": v(-248.31, -8.15) * mm, "end": v(-247.2, -12.3) * mm});
            skLineSegment(sketch, "E649.MirrorCS", {"start": v(-293.36, 6.35) * mm, "end": v(-299.6, 10.73) * mm});
            skArc(sketch, "E650.MirrorCS", {"start": v(-187.33, 45.84) * mm, "mid": v(-184.57, 49.13) * mm, "end": v(-180.28, 49.13) * mm});
            skLineSegment(sketch, "E651.MirrorCS", {"start": v(-325.22, 6.8) * mm, "end": v(-311.97, 12.98) * mm});
            skArc(sketch, "E652.MirrorCS", {"start": v(-273.28, -4.02) * mm, "mid": v(-270.52, -7.3) * mm, "end": v(-271.26, -11.54) * mm});
            skLineSegment(sketch, "E653.MirrorCS", {"start": v(-200.98, 20.5) * mm, "end": v(-196.6, 26.74) * mm});
            skLineSegment(sketch, "E654.MirrorCS", {"start": v(-237.39, -3.96) * mm, "end": v(-230.23, -1.35) * mm});
            skLineSegment(sketch, "E655.MirrorCS", {"start": v(-321.63, 38.48) * mm, "end": v(-323.6, 45.84) * mm});
            skLineSegment(sketch, "E656.MirrorCS", {"start": v(-188.85, 27.42) * mm, "end": v(-178.5, 17.08) * mm});
            skLineSegment(sketch, "E657.MirrorCS", {"start": v(-223.49, -5.25) * mm, "end": v(-220.95, -19.65) * mm});
            skArc(sketch, "E658.MirrorCS", {"start": v(-343.9, 42.95) * mm, "mid": v(-346.37, 40.5) * mm, "end": v(-346.67, 37.03) * mm});
            skLineSegment(sketch, "E659.MirrorCS", {"start": v(-330.65, 49.13) * mm, "end": v(-343.9, 42.95) * mm});
            skLineSegment(sketch, "E660.MirrorCS", {"start": v(-185.7, 6.8) * mm, "end": v(-198.96, 12.98) * mm});
            skLineSegment(sketch, "E661.MirrorCS", {"start": v(-232.74, -23.94) * mm, "end": v(-240.05, -11.27) * mm});
            skArc(sketch, "E662.MirrorCS", {"start": v(-313.3, -4.55) * mm, "mid": v(-313.6, -8) * mm, "end": v(-311.6, -10.85) * mm});
            skLineSegment(sketch, "E663.MirrorCS", {"start": v(-307.12, 8.71) * mm, "end": v(-313.3, -4.55) * mm});
            skArc(sketch, "E664.MirrorCS", {"start": v(-198.96, 12.98) * mm, "mid": v(-201.72, 16.27) * mm, "end": v(-200.98, 20.5) * mm});
            skArc(sketch, "E665.MirrorCS", {"start": v(-240.05, -11.27) * mm, "mid": v(-240.42, -7) * mm, "end": v(-237.39, -3.96) * mm});
            skArc(sketch, "E666.MirrorCS", {"start": v(-179.4, 8.49) * mm, "mid": v(-182.24, 6.5) * mm, "end": v(-185.7, 6.8) * mm});
            skArc(sketch, "E667.MirrorCS", {"start": v(-226.6, -26.18) * mm, "mid": v(-230.07, -26.18) * mm, "end": v(-232.74, -23.94) * mm});
            skLineSegment(sketch, "E668.MirrorCS", {"start": v(-322.08, 27.42) * mm, "end": v(-332.42, 17.08) * mm});
            skLineSegment(sketch, "E669.MirrorCS", {"start": v(-303.02, -11.74) * mm, "end": v(-292.68, -1.4) * mm});
            skArc(sketch, "E670.MirrorCS", {"start": v(-309.53, -12.31) * mm, "mid": v(-306.17, -13.21) * mm, "end": v(-303.02, -11.74) * mm});
            skLineSegment(sketch, "E671.MirrorCS", {"start": v(-340.66, 30.83) * mm, "end": v(-326.09, 32.1) * mm});
            skArc(sketch, "E672.MirrorCS", {"start": v(-220.95, -19.65) * mm, "mid": v(-221.55, -23.07) * mm, "end": v(-224.21, -25.3) * mm});
            skArc(sketch, "E673.MirrorCS", {"start": v(-346.01, 34.58) * mm, "mid": v(-344.02, 31.73) * mm, "end": v(-340.66, 30.83) * mm});
            skArc(sketch, "E674.MirrorCS", {"start": v(-292.68, -1.4) * mm, "mid": v(-291.2, 2.64) * mm, "end": v(-293.36, 6.35) * mm});
            skPoint(sketch, "E675.visualSharp", {"position": v(8.94, 152.88) * mm});
            skLineSegment(sketch, "E675.filletArc", {"start": v(8.94, 152.88) * mm, "end": v(8.94, 152.88) * mm});
            skSolve(sketch);
        }
        {
            var Q0;
            {var subQ15=sQuery(id+"F0.wireOp",EDGE,"E206.MirrorCS");Q0=makeQuery(id+"F0.imprint","IMPRINT",FACE,{"disambiguationData":[TD([[makeQuery(id+"F0.imprint","IMPRINT",EDGE,{"derivedFrom":subQ15}),1.0]])]});}
            var Q1;
            {var subQ14=sQuery(id+"F0.wireOp",EDGE,"E159.MirrorCS");Q1=makeQuery(id+"F0.imprint","IMPRINT",FACE,{"disambiguationData":[TD([[makeQuery(id+"F0.imprint","IMPRINT",EDGE,{"derivedFrom":subQ14}),1.0]])]});}
            var Q2;
            {var subQ1=sQuery(id+"F0.wireOp",EDGE,"E210.MirrorCS");Q2=makeQuery(id+"F0.imprint","IMPRINT",FACE,{"disambiguationData":[TD([[makeQuery(id+"F0.imprint","IMPRINT",EDGE,{"derivedFrom":subQ1}),1.0]])]});}
            var Q3;
            {var subQ17=sQuery(id+"F0.wireOp",EDGE,"E112");Q3=makeQuery(id+"F0.imprint","IMPRINT",FACE,{"disambiguationData":[TD([[makeQuery(id+"F0.imprint","IMPRINT",EDGE,{"derivedFrom":subQ17}),-1.0]])]});}
            var Q4;
            {var subQ1=sQuery(id+"F0.wireOp",EDGE,"E185");Q4=makeQuery(id+"F0.imprint","IMPRINT",FACE,{"disambiguationData":[TD([[makeQuery(id+"F0.imprint","IMPRINT",EDGE,{"derivedFrom":subQ1}),1.0]])]});}
            var Q5;
            Q5=makeQuery(id+"F0.imprint","IMPRINT",FACE,{"disambiguationData":[TD([[makeQuery(id+"F0.imprint","IMPRINT",EDGE,{"derivedFrom":sQuery(id+"F0.wireOp",EDGE,"E193.MirrorCS")}),-1.0]])]});
            var Q6;
            {var subQ5=sQuery(id+"F0.wireOp",EDGE,"E152.MirrorCS");Q6=makeQuery(id+"F0.imprint","IMPRINT",FACE,{"disambiguationData":[TD([[makeQuery(id+"F0.imprint","IMPRINT",EDGE,{"derivedFrom":subQ5}),-1.0]])]});}
            var Q7;
            {var subQ4=sQuery(id+"F0.wireOp",EDGE,"E145");Q7=makeQuery(id+"F0.imprint","IMPRINT",FACE,{"disambiguationData":[TD([[makeQuery(id+"F0.imprint","IMPRINT",EDGE,{"derivedFrom":subQ4}),1.0]])]});}
            var Q8;
            Q8=makeQuery(id+"F0.imprint","IMPRINT",FACE,{"disambiguationData":[TD([[makeQuery(id+"F0.imprint","IMPRINT",EDGE,{"derivedFrom":sQuery(id+"F0.wireOp",EDGE,"E198.MirrorCS")}),1.0]])]});
            var Q9;
            Q9=makeQuery(id+"F0.imprint","IMPRINT",FACE,{"disambiguationData":[TD([[makeQuery(id+"F0.imprint","IMPRINT",EDGE,{"derivedFrom":sQuery(id+"F0.wireOp",EDGE,"E200.MirrorCS")}),-1.0]])]});
            var Q10;
            Q10=makeQuery(id+"F0.imprint","IMPRINT",FACE,{"disambiguationData":[TD([[makeQuery(id+"F0.imprint","IMPRINT",EDGE,{"derivedFrom":sQuery(id+"F0.wireOp",EDGE,"E199.MirrorCS")}),-1.0]])]});
            var Q11;
            Q11=makeQuery(id+"F0.imprint","IMPRINT",FACE,{"disambiguationData":[TD([[makeQuery(id+"F0.imprint","IMPRINT",EDGE,{"derivedFrom":sQuery(id+"F0.wireOp",EDGE,"E194.MirrorCS")}),-1.0]])]});
            var Q12;
            Q12=makeQuery(id+"F0.imprint","IMPRINT",FACE,{"disambiguationData":[TD([[makeQuery(id+"F0.imprint","IMPRINT",EDGE,{"derivedFrom":sQuery(id+"F0.wireOp",EDGE,"E196.MirrorCS")}),-1.0]])]});
            var Q13;
            {var subQ1=sQuery(id+"F0.wireOp",EDGE,"E129");Q13=makeQuery(id+"F0.imprint","IMPRINT",FACE,{"disambiguationData":[TD([[makeQuery(id+"F0.imprint","IMPRINT",EDGE,{"derivedFrom":subQ1}),1.0]])]});}
            var Q14;
            Q14=makeQuery(id+"F0.imprint","IMPRINT",FACE,{"disambiguationData":[TD([[makeQuery(id+"F0.imprint","IMPRINT",EDGE,{"derivedFrom":sQuery(id+"F0.wireOp",EDGE,"E197.MirrorCS")}),1.0]])]});
            var Q15;
            {var subQ6=sQuery(id+"F0.wireOp",EDGE,"E220.MirrorCS");Q15=makeQuery(id+"F0.imprint","IMPRINT",FACE,{"disambiguationData":[TD([[makeQuery(id+"F0.imprint","IMPRINT",EDGE,{"derivedFrom":subQ6}),-1.0]])]});}
            var Q16;
            {var subQ5=sQuery(id+"F0.wireOp",EDGE,"E128");Q16=makeQuery(id+"F0.imprint","IMPRINT",FACE,{"disambiguationData":[TD([[makeQuery(id+"F0.imprint","IMPRINT",EDGE,{"derivedFrom":subQ5}),1.0]])]});}
            var Q17;
            {var subQ5=sQuery(id+"F0.wireOp",EDGE,"E243.MirrorCS");Q17=makeQuery(id+"F0.imprint","IMPRINT",FACE,{"disambiguationData":[TD([[makeQuery(id+"F0.imprint","IMPRINT",EDGE,{"derivedFrom":subQ5}),-1.0]])]});}
            var Q18;
            {var subQ5=sQuery(id+"F0.wireOp",EDGE,"E159.MirrorCS");Q18=makeQuery(id+"F0.imprint","IMPRINT",FACE,{"disambiguationData":[TD([[makeQuery(id+"F0.imprint","IMPRINT",EDGE,{"derivedFrom":subQ5}),-1.0]])]});}
            var Q19;
            {var subQ1=sQuery(id+"F0.wireOp",EDGE,"E113");Q19=makeQuery(id+"F0.imprint","IMPRINT",FACE,{"disambiguationData":[TD([[makeQuery(id+"F0.imprint","IMPRINT",EDGE,{"derivedFrom":subQ1}),1.0]])]});}
            var Q20;
            {var subQ4=sQuery(id+"F0.wireOp",EDGE,"E213.MirrorCS");Q20=makeQuery(id+"F0.imprint","IMPRINT",FACE,{"disambiguationData":[TD([[makeQuery(id+"F0.imprint","IMPRINT",EDGE,{"derivedFrom":subQ4}),-1.0]])]});}
            var Q21;
            Q21=makeQuery(id+"F0.imprint","IMPRINT",FACE,{"disambiguationData":[TD([[makeQuery(id+"F0.imprint","IMPRINT",EDGE,{"derivedFrom":sQuery(id+"F0.wireOp",EDGE,"E153.MirrorCS")}),-1.0]])]});
            var Q22;
            {var subQ5=sQuery(id+"F0.wireOp",EDGE,"E170.MirrorCS");Q22=makeQuery(id+"F0.imprint","IMPRINT",FACE,{"disambiguationData":[TD([[makeQuery(id+"F0.imprint","IMPRINT",EDGE,{"derivedFrom":subQ5}),-1.0]])]});}
            var Q23;
            {var subQ5=sQuery(id+"F0.wireOp",EDGE,"E120");Q23=makeQuery(id+"F0.imprint","IMPRINT",FACE,{"disambiguationData":[TD([[makeQuery(id+"F0.imprint","IMPRINT",EDGE,{"derivedFrom":subQ5}),1.0]])]});}
            var Q24;
            {var subQ5=sQuery(id+"F0.wireOp",EDGE,"E242.MirrorCS");Q24=makeQuery(id+"F0.imprint","IMPRINT",FACE,{"disambiguationData":[TD([[makeQuery(id+"F0.imprint","IMPRINT",EDGE,{"derivedFrom":subQ5}),-1.0]])]});}
            var Q25;
            {var subQ0=sQuery(id+"F0.wireOp",EDGE,"E137");Q25=makeQuery(id+"F0.imprint","IMPRINT",FACE,{"disambiguationData":[TD([[makeQuery(id+"F0.imprint","IMPRINT",EDGE,{"derivedFrom":subQ0}),1.0]])]});}
            var Q26;
            {var subQ0=sQuery(id+"F0.wireOp",EDGE,"E105");Q26=makeQuery(id+"F0.imprint","IMPRINT",FACE,{"disambiguationData":[TD([[makeQuery(id+"F0.imprint","IMPRINT",EDGE,{"derivedFrom":subQ0}),1.0]])]});}
            var Q27;
            {var subQ0=sQuery(id+"F0.wireOp",EDGE,"E183.MirrorCS");Q27=makeQuery(id+"F0.imprint","IMPRINT",FACE,{"disambiguationData":[TD([[makeQuery(id+"F0.imprint","IMPRINT",EDGE,{"derivedFrom":subQ0}),-1.0]])]});}
            var Q28;
            Q28=makeQuery(id+"F0.imprint","IMPRINT",FACE,{"disambiguationData":[TD([[makeQuery(id+"F0.imprint","IMPRINT",EDGE,{"derivedFrom":sQuery(id+"F0.wireOp",EDGE,"E155.MirrorCS")}),-1.0]])]});
            var Q29;
            {var subQ5=sQuery(id+"F0.wireOp",EDGE,"E160.MirrorCS");Q29=makeQuery(id+"F0.imprint","IMPRINT",FACE,{"disambiguationData":[TD([[makeQuery(id+"F0.imprint","IMPRINT",EDGE,{"derivedFrom":subQ5}),-1.0]])]});}
            var Q30;
            Q30=makeQuery(id+"F0.imprint","IMPRINT",FACE,{"disambiguationData":[TD([[makeQuery(id+"F0.imprint","IMPRINT",EDGE,{"derivedFrom":sQuery(id+"F0.wireOp",EDGE,"E192.MirrorCS")}),1.0]])]});
            var Q31;
            {var subQ5=sQuery(id+"F0.wireOp",EDGE,"E216.MirrorCS");Q31=makeQuery(id+"F0.imprint","IMPRINT",FACE,{"disambiguationData":[TD([[makeQuery(id+"F0.imprint","IMPRINT",EDGE,{"derivedFrom":subQ5}),1.0]])]});}
            var Q32;
            Q32=makeQuery(id+"F0.imprint","IMPRINT",FACE,{"disambiguationData":[TD([[makeQuery(id+"F0.imprint","IMPRINT",EDGE,{"derivedFrom":sQuery(id+"F0.wireOp",EDGE,"E161.MirrorCS")}),-1.0]])]});
            var Q33;
            {var subQ5=sQuery(id+"F0.wireOp",EDGE,"E184");Q33=makeQuery(id+"F0.imprint","IMPRINT",FACE,{"disambiguationData":[TD([[makeQuery(id+"F0.imprint","IMPRINT",EDGE,{"derivedFrom":subQ5}),1.0]])]});}
            var Q34;
            {var subQ0=sQuery(id+"F0.wireOp",EDGE,"E107");Q34=makeQuery(id+"F0.imprint","IMPRINT",FACE,{"disambiguationData":[TD([[makeQuery(id+"F0.imprint","IMPRINT",EDGE,{"derivedFrom":subQ0}),1.0]])]});}
            var Q35;
            {var subQ5=sQuery(id+"F0.wireOp",EDGE,"E238.MirrorCS");Q35=makeQuery(id+"F0.imprint","IMPRINT",FACE,{"disambiguationData":[TD([[makeQuery(id+"F0.imprint","IMPRINT",EDGE,{"derivedFrom":subQ5}),1.0]])]});}
            var Q36;
            {var subQ5=sQuery(id+"F0.wireOp",EDGE,"E207.MirrorCS");Q36=makeQuery(id+"F0.imprint","IMPRINT",FACE,{"disambiguationData":[TD([[makeQuery(id+"F0.imprint","IMPRINT",EDGE,{"derivedFrom":subQ5}),-1.0]])]});}
            var Q37;
            {var subQ0=sQuery(id+"F0.wireOp",EDGE,"E237.MirrorCS");var subQ1=sQuery(id+"F0.wireOp",EDGE,"E2");var subQ2=makeQuery(id+"F0.imprint","INTERSECT",VERTEX,{"derivedFrom":[subQ1,subQ0]});Q37=makeQuery(id+"F0.imprint","IMPRINT",FACE,{"disambiguationData":[TD([[makeQuery(id+"F0.imprint","IMPRINT",EDGE,{"disambiguationData":[TD([[subQ2,1.0]])],"derivedFrom":subQ1}),1.0]])]});}
            var Q38;
            {var subQ1=sQuery(id+"F0.wireOp",EDGE,"E121");Q38=makeQuery(id+"F0.imprint","IMPRINT",FACE,{"disambiguationData":[TD([[makeQuery(id+"F0.imprint","IMPRINT",EDGE,{"derivedFrom":subQ1}),1.0]])]});}
            var Q39;
            {var subQ5=sQuery(id+"F0.wireOp",EDGE,"E210.MirrorCS");Q39=makeQuery(id+"F0.imprint","IMPRINT",FACE,{"disambiguationData":[TD([[makeQuery(id+"F0.imprint","IMPRINT",EDGE,{"derivedFrom":subQ5}),-1.0]])]});}
            var Q40;
            {var subQ5=sQuery(id+"F0.wireOp",EDGE,"E244.MirrorCS");Q40=makeQuery(id+"F0.imprint","IMPRINT",FACE,{"disambiguationData":[TD([[makeQuery(id+"F0.imprint","IMPRINT",EDGE,{"derivedFrom":subQ5}),1.0]])]});}
            var Q41;
            {var subQ0=sQuery(id+"F0.wireOp",EDGE,"E110.filletArc");var subQ1=sQuery(id+"F0.wireOp",EDGE,"E2");var subQ2=makeQuery(id+"F0.imprint","INTERSECT",VERTEX,{"derivedFrom":[subQ1,subQ0]});Q41=makeQuery(id+"F0.imprint","IMPRINT",FACE,{"disambiguationData":[TD([[makeQuery(id+"F0.imprint","IMPRINT",EDGE,{"disambiguationData":[TD([[subQ2,1.0]])],"derivedFrom":subQ1}),1.0]])]});}
            var Q42;
            {var subQ0=sQuery(id+"F0.wireOp",EDGE,"E103");var subQ1=sQuery(id+"F0.wireOp",EDGE,"E2");var subQ2=makeQuery(id+"F0.imprint","INTERSECT",VERTEX,{"disambiguationData":[OD(0.0)],"derivedFrom":[subQ1,subQ0]});Q42=makeQuery(id+"F0.imprint","IMPRINT",FACE,{"disambiguationData":[TD([[makeQuery(id+"F0.imprint","IMPRINT",EDGE,{"disambiguationData":[TD([[subQ2,1.0]])],"derivedFrom":subQ1}),1.0]])]});}
            var Q43;
            {var subQ0=sQuery(id+"F0.wireOp",EDGE,"E150.filletArc");var subQ1=sQuery(id+"F0.wireOp",EDGE,"E2");var subQ2=makeQuery(id+"F0.imprint","INTERSECT",VERTEX,{"derivedFrom":[subQ1,subQ0]});Q43=makeQuery(id+"F0.imprint","IMPRINT",FACE,{"disambiguationData":[TD([[makeQuery(id+"F0.imprint","IMPRINT",EDGE,{"disambiguationData":[TD([[subQ2,1.0]])],"derivedFrom":subQ1}),1.0]])]});}
            var Q44;
            {var subQ5=sQuery(id+"F0.wireOp",EDGE,"E206.MirrorCS");Q44=makeQuery(id+"F0.imprint","IMPRINT",FACE,{"disambiguationData":[TD([[makeQuery(id+"F0.imprint","IMPRINT",EDGE,{"derivedFrom":subQ5}),-1.0]])]});}
            var Q45;
            {var subQ5=sQuery(id+"F0.wireOp",EDGE,"E136");Q45=makeQuery(id+"F0.imprint","IMPRINT",FACE,{"disambiguationData":[TD([[makeQuery(id+"F0.imprint","IMPRINT",EDGE,{"derivedFrom":subQ5}),1.0]])]});}
            var Q46;
            {var subQ5=sQuery(id+"F0.wireOp",EDGE,"E112");Q46=makeQuery(id+"F0.imprint","IMPRINT",FACE,{"disambiguationData":[TD([[makeQuery(id+"F0.imprint","IMPRINT",EDGE,{"derivedFrom":subQ5}),1.0]])]});}
            var Q47;
            {var subQ0=sQuery(id+"F0.wireOp",EDGE,"E177.MirrorCS");var subQ1=sQuery(id+"F0.wireOp",EDGE,"E2");var subQ2=makeQuery(id+"F0.imprint","INTERSECT",VERTEX,{"derivedFrom":[subQ1,subQ0]});Q47=makeQuery(id+"F0.imprint","IMPRINT",FACE,{"disambiguationData":[TD([[makeQuery(id+"F0.imprint","IMPRINT",EDGE,{"disambiguationData":[TD([[subQ2,1.0]])],"derivedFrom":subQ1}),1.0]])]});}
            var Q48;
            {var subQ0=sQuery(id+"F0.wireOp",EDGE,"E232.MirrorCS");var subQ1=sQuery(id+"F0.wireOp",EDGE,"E2");var subQ2=makeQuery(id+"F0.imprint","INTERSECT",VERTEX,{"derivedFrom":[subQ1,subQ0]});Q48=makeQuery(id+"F0.imprint","IMPRINT",FACE,{"disambiguationData":[TD([[makeQuery(id+"F0.imprint","IMPRINT",EDGE,{"disambiguationData":[TD([[subQ2,-1.0]])],"derivedFrom":subQ1}),1.0]])]});}
            var Q49;
            {var subQ0=sQuery(id+"F0.wireOp",EDGE,"E111.filletArc");var subQ1=sQuery(id+"F0.wireOp",EDGE,"E2");var subQ2=makeQuery(id+"F0.imprint","INTERSECT",VERTEX,{"derivedFrom":[subQ1,subQ0]});Q49=makeQuery(id+"F0.imprint","IMPRINT",FACE,{"disambiguationData":[TD([[makeQuery(id+"F0.imprint","IMPRINT",EDGE,{"disambiguationData":[TD([[subQ2,-1.0]])],"derivedFrom":subQ1}),1.0]])]});}
            var Q50;
            {var subQ0=sQuery(id+"F0.wireOp",EDGE,"E156.MirrorCS");var subQ1=sQuery(id+"F0.wireOp",EDGE,"E2");var subQ2=makeQuery(id+"F0.imprint","INTERSECT",VERTEX,{"derivedFrom":[subQ1,subQ0]});Q50=makeQuery(id+"F0.imprint","IMPRINT",FACE,{"disambiguationData":[TD([[makeQuery(id+"F0.imprint","IMPRINT",EDGE,{"disambiguationData":[TD([[subQ2,-1.0]])],"derivedFrom":subQ1}),1.0]])]});}
            extrude(context, id + "F1", {"entities" : qUnion([Q0, Q1, Q2, Q3, Q4, Q5, Q6, Q7, Q8, Q9, Q10, Q11, Q12, Q13, Q14, Q15, Q16, Q17, Q18, Q19, Q20, Q21, Q22, Q23, Q24, Q25, Q26, Q27, Q28, Q29, Q30, Q31, Q32, Q33, Q34, Q35, Q36, Q37, Q38, Q39, Q40, Q41, Q42, Q43, Q44, Q45, Q46, Q47, Q48, Q49, Q50]), "depth" : 6.35 * mm});
        }
        {
            var Q0;
            {var subQ103=sQuery(id+"F0.wireOp",EDGE,"E4");Q0=makeQuery(id+"F0.imprint","IMPRINT",FACE,{"disambiguationData":[TD([[makeQuery(id+"F0.imprint","IMPRINT",EDGE,{"derivedFrom":subQ103}),-1.0]])]});}
            var Q1;
            {var subQ1=sQuery(id+"F0.wireOp",EDGE,"E69");Q1=makeQuery(id+"F0.imprint","IMPRINT",FACE,{"disambiguationData":[TD([[makeQuery(id+"F0.imprint","IMPRINT",EDGE,{"derivedFrom":subQ1}),1.0]])]});}
            var Q2;
            {var subQ5=sQuery(id+"F0.wireOp",EDGE,"E68");Q2=makeQuery(id+"F0.imprint","IMPRINT",FACE,{"disambiguationData":[TD([[makeQuery(id+"F0.imprint","IMPRINT",EDGE,{"derivedFrom":subQ5}),1.0]])]});}
            var Q3;
            {var subQ0=sQuery(id+"F0.wireOp",EDGE,"E61");Q3=makeQuery(id+"F0.imprint","IMPRINT",FACE,{"disambiguationData":[TD([[makeQuery(id+"F0.imprint","IMPRINT",EDGE,{"derivedFrom":subQ0}),1.0]])]});}
            var Q4;
            {var subQ5=sQuery(id+"F0.wireOp",EDGE,"E60");Q4=makeQuery(id+"F0.imprint","IMPRINT",FACE,{"disambiguationData":[TD([[makeQuery(id+"F0.imprint","IMPRINT",EDGE,{"derivedFrom":subQ5}),1.0]])]});}
            var Q5;
            {var subQ6=sQuery(id+"F0.wireOp",EDGE,"E53");Q5=makeQuery(id+"F0.imprint","IMPRINT",FACE,{"disambiguationData":[TD([[makeQuery(id+"F0.imprint","IMPRINT",EDGE,{"derivedFrom":subQ6}),1.0]])]});}
            var Q6;
            {var subQ5=sQuery(id+"F0.wireOp",EDGE,"E52");Q6=makeQuery(id+"F0.imprint","IMPRINT",FACE,{"disambiguationData":[TD([[makeQuery(id+"F0.imprint","IMPRINT",EDGE,{"derivedFrom":subQ5}),1.0]])]});}
            var Q7;
            {var subQ6=sQuery(id+"F0.wireOp",EDGE,"E45");Q7=makeQuery(id+"F0.imprint","IMPRINT",FACE,{"disambiguationData":[TD([[makeQuery(id+"F0.imprint","IMPRINT",EDGE,{"derivedFrom":subQ6}),1.0]])]});}
            var Q8;
            {var subQ5=sQuery(id+"F0.wireOp",EDGE,"E44");Q8=makeQuery(id+"F0.imprint","IMPRINT",FACE,{"disambiguationData":[TD([[makeQuery(id+"F0.imprint","IMPRINT",EDGE,{"derivedFrom":subQ5}),1.0]])]});}
            var Q9;
            {var subQ1=sQuery(id+"F0.wireOp",EDGE,"E37");Q9=makeQuery(id+"F0.imprint","IMPRINT",FACE,{"disambiguationData":[TD([[makeQuery(id+"F0.imprint","IMPRINT",EDGE,{"derivedFrom":subQ1}),1.0]])]});}
            var Q10;
            {var subQ5=sQuery(id+"F0.wireOp",EDGE,"E36");Q10=makeQuery(id+"F0.imprint","IMPRINT",FACE,{"disambiguationData":[TD([[makeQuery(id+"F0.imprint","IMPRINT",EDGE,{"derivedFrom":subQ5}),1.0]])]});}
            var Q11;
            {var subQ1=sQuery(id+"F0.wireOp",EDGE,"E29");Q11=makeQuery(id+"F0.imprint","IMPRINT",FACE,{"disambiguationData":[TD([[makeQuery(id+"F0.imprint","IMPRINT",EDGE,{"derivedFrom":subQ1}),1.0]])]});}
            var Q12;
            {var subQ5=sQuery(id+"F0.wireOp",EDGE,"E28");Q12=makeQuery(id+"F0.imprint","IMPRINT",FACE,{"disambiguationData":[TD([[makeQuery(id+"F0.imprint","IMPRINT",EDGE,{"derivedFrom":subQ5}),1.0]])]});}
            var Q13;
            {var subQ0=sQuery(id+"F0.wireOp",EDGE,"E21");Q13=makeQuery(id+"F0.imprint","IMPRINT",FACE,{"disambiguationData":[TD([[makeQuery(id+"F0.imprint","IMPRINT",EDGE,{"derivedFrom":subQ0}),1.0]])]});}
            var Q14;
            {var subQ5=sQuery(id+"F0.wireOp",EDGE,"E20");Q14=makeQuery(id+"F0.imprint","IMPRINT",FACE,{"disambiguationData":[TD([[makeQuery(id+"F0.imprint","IMPRINT",EDGE,{"derivedFrom":subQ5}),1.0]])]});}
            var Q15;
            {var subQ5=sQuery(id+"F0.wireOp",EDGE,"E12");Q15=makeQuery(id+"F0.imprint","IMPRINT",FACE,{"disambiguationData":[TD([[makeQuery(id+"F0.imprint","IMPRINT",EDGE,{"derivedFrom":subQ5}),1.0]])]});}
            var Q16;
            {var subQ1=sQuery(id+"F0.wireOp",EDGE,"uNHU9NjM-voS0-thDM-VK8L-I11DhVX6XWQf");Q16=makeQuery(id+"F0.imprint","IMPRINT",FACE,{"disambiguationData":[TD([[makeQuery(id+"F0.imprint","IMPRINT",EDGE,{"derivedFrom":subQ1}),1.0]])]});}
            var Q17;
            {var subQ0=sQuery(id+"F0.wireOp",EDGE,"E9.filletArc");var subQ1=sQuery(id+"F0.wireOp",EDGE,"E0");var subQ2=makeQuery(id+"F0.imprint","INTERSECT",VERTEX,{"derivedFrom":[subQ1,subQ0]});Q17=makeQuery(id+"F0.imprint","IMPRINT",FACE,{"disambiguationData":[TD([[makeQuery(id+"F0.imprint","IMPRINT",EDGE,{"disambiguationData":[TD([[subQ2,-1.0]])],"derivedFrom":subQ1}),1.0]])]});}
            var Q18;
            Q18=makeQuery(id+"F0.imprint","IMPRINT",FACE,{"disambiguationData":[TD([[makeQuery(id+"F0.imprint","IMPRINT",EDGE,{"derivedFrom":sQuery(id+"F0.wireOp",EDGE,"E286.MirrorCS")}),-1.0]])]});
            var Q19;
            {var subQ5=sQuery(id+"F0.wireOp",EDGE,"E308.MirrorCS");Q19=makeQuery(id+"F0.imprint","IMPRINT",FACE,{"disambiguationData":[TD([[makeQuery(id+"F0.imprint","IMPRINT",EDGE,{"derivedFrom":subQ5}),-1.0]])]});}
            var Q20;
            Q20=makeQuery(id+"F0.imprint","IMPRINT",FACE,{"disambiguationData":[TD([[makeQuery(id+"F0.imprint","IMPRINT",EDGE,{"derivedFrom":sQuery(id+"F0.wireOp",EDGE,"E285.MirrorCS")}),-1.0]])]});
            var Q21;
            {var subQ5=sQuery(id+"F0.wireOp",EDGE,"E267.MirrorCS");Q21=makeQuery(id+"F0.imprint","IMPRINT",FACE,{"disambiguationData":[TD([[makeQuery(id+"F0.imprint","IMPRINT",EDGE,{"derivedFrom":subQ5}),-1.0]])]});}
            var Q22;
            Q22=makeQuery(id+"F0.imprint","IMPRINT",FACE,{"disambiguationData":[TD([[makeQuery(id+"F0.imprint","IMPRINT",EDGE,{"derivedFrom":sQuery(id+"F0.wireOp",EDGE,"E290.MirrorCS")}),-1.0]])]});
            var Q23;
            {var subQ5=sQuery(id+"F0.wireOp",EDGE,"E274.MirrorCS");Q23=makeQuery(id+"F0.imprint","IMPRINT",FACE,{"disambiguationData":[TD([[makeQuery(id+"F0.imprint","IMPRINT",EDGE,{"derivedFrom":subQ5}),-1.0]])]});}
            var Q24;
            Q24=makeQuery(id+"F0.imprint","IMPRINT",FACE,{"disambiguationData":[TD([[makeQuery(id+"F0.imprint","IMPRINT",EDGE,{"derivedFrom":sQuery(id+"F0.wireOp",EDGE,"E265.MirrorCS")}),-1.0]])]});
            var Q25;
            {var subQ5=sQuery(id+"F0.wireOp",EDGE,"E291.MirrorCS");Q25=makeQuery(id+"F0.imprint","IMPRINT",FACE,{"disambiguationData":[TD([[makeQuery(id+"F0.imprint","IMPRINT",EDGE,{"derivedFrom":subQ5}),-1.0]])]});}
            var Q26;
            Q26=makeQuery(id+"F0.imprint","IMPRINT",FACE,{"disambiguationData":[TD([[makeQuery(id+"F0.imprint","IMPRINT",EDGE,{"derivedFrom":sQuery(id+"F0.wireOp",EDGE,"E266.MirrorCS")}),-1.0]])]});
            var Q27;
            {var subQ5=sQuery(id+"F0.wireOp",EDGE,"E297.MirrorCS");Q27=makeQuery(id+"F0.imprint","IMPRINT",FACE,{"disambiguationData":[TD([[makeQuery(id+"F0.imprint","IMPRINT",EDGE,{"derivedFrom":subQ5}),-1.0]])]});}
            var Q28;
            {var subQ0=sQuery(id+"F0.wireOp",EDGE,"E276.MirrorCS");Q28=makeQuery(id+"F0.imprint","IMPRINT",FACE,{"disambiguationData":[TD([[makeQuery(id+"F0.imprint","IMPRINT",EDGE,{"derivedFrom":subQ0}),-1.0]])]});}
            var Q29;
            {var subQ2=sQuery(id+"F0.wireOp",EDGE,"E268.MirrorCS");Q29=makeQuery(id+"F0.imprint","IMPRINT",FACE,{"disambiguationData":[TD([[makeQuery(id+"F0.imprint","IMPRINT",EDGE,{"derivedFrom":subQ2}),-1.0]])]});}
            var Q30;
            Q30=makeQuery(id+"F0.imprint","IMPRINT",FACE,{"disambiguationData":[TD([[makeQuery(id+"F0.imprint","IMPRINT",EDGE,{"derivedFrom":sQuery(id+"F0.wireOp",EDGE,"E278.MirrorCS")}),-1.0]])]});
            var Q31;
            {var subQ5=sQuery(id+"F0.wireOp",EDGE,"E311.MirrorCS");Q31=makeQuery(id+"F0.imprint","IMPRINT",FACE,{"disambiguationData":[TD([[makeQuery(id+"F0.imprint","IMPRINT",EDGE,{"derivedFrom":subQ5}),-1.0]])]});}
            var Q32;
            Q32=makeQuery(id+"F0.imprint","IMPRINT",FACE,{"disambiguationData":[TD([[makeQuery(id+"F0.imprint","IMPRINT",EDGE,{"derivedFrom":sQuery(id+"F0.wireOp",EDGE,"E293.MirrorCS")}),-1.0]])]});
            var Q33;
            {var subQ5=sQuery(id+"F0.wireOp",EDGE,"E304.MirrorCS");Q33=makeQuery(id+"F0.imprint","IMPRINT",FACE,{"disambiguationData":[TD([[makeQuery(id+"F0.imprint","IMPRINT",EDGE,{"derivedFrom":subQ5}),-1.0]])]});}
            var Q34;
            {var subQ0=sQuery(id+"F0.wireOp",EDGE,"E296.MirrorCS");Q34=makeQuery(id+"F0.imprint","IMPRINT",FACE,{"disambiguationData":[TD([[makeQuery(id+"F0.imprint","IMPRINT",EDGE,{"derivedFrom":subQ0}),-1.0]])]});}
            var Q35;
            {var subQ1=sQuery(id+"F0.wireOp",EDGE,"E269.MirrorCS");Q35=makeQuery(id+"F0.imprint","IMPRINT",FACE,{"disambiguationData":[TD([[makeQuery(id+"F0.imprint","IMPRINT",EDGE,{"derivedFrom":subQ1}),-1.0]])]});}
            var Q36;
            Q36=makeQuery(id+"F0.imprint","IMPRINT",FACE,{"disambiguationData":[TD([[makeQuery(id+"F0.imprint","IMPRINT",EDGE,{"derivedFrom":sQuery(id+"F0.wireOp",EDGE,"E272.MirrorCS")}),-1.0]])]});
            var Q37;
            {var subQ5=sQuery(id+"F0.wireOp",EDGE,"E280.MirrorCS");Q37=makeQuery(id+"F0.imprint","IMPRINT",FACE,{"disambiguationData":[TD([[makeQuery(id+"F0.imprint","IMPRINT",EDGE,{"derivedFrom":subQ5}),-1.0]])]});}
            var Q38;
            Q38=makeQuery(id+"F0.imprint","IMPRINT",FACE,{"disambiguationData":[TD([[makeQuery(id+"F0.imprint","IMPRINT",EDGE,{"derivedFrom":sQuery(id+"F0.wireOp",EDGE,"E394.MirrorCS")}),1.0]])]});
            var Q39;
            {var subQ5=sQuery(id+"F0.wireOp",EDGE,"E440.MirrorCS");Q39=makeQuery(id+"F0.imprint","IMPRINT",FACE,{"disambiguationData":[TD([[makeQuery(id+"F0.imprint","IMPRINT",EDGE,{"derivedFrom":subQ5}),1.0]])]});}
            var Q40;
            Q40=makeQuery(id+"F0.imprint","IMPRINT",FACE,{"disambiguationData":[TD([[makeQuery(id+"F0.imprint","IMPRINT",EDGE,{"derivedFrom":sQuery(id+"F0.wireOp",EDGE,"E364.MirrorCS")}),1.0]])]});
            var Q41;
            {var subQ5=sQuery(id+"F0.wireOp",EDGE,"E360.MirrorCS");Q41=makeQuery(id+"F0.imprint","IMPRINT",FACE,{"disambiguationData":[TD([[makeQuery(id+"F0.imprint","IMPRINT",EDGE,{"derivedFrom":subQ5}),1.0]])]});}
            var Q42;
            Q42=makeQuery(id+"F0.imprint","IMPRINT",FACE,{"disambiguationData":[TD([[makeQuery(id+"F0.imprint","IMPRINT",EDGE,{"derivedFrom":sQuery(id+"F0.wireOp",EDGE,"E369.MirrorCS")}),1.0]])]});
            var Q43;
            {var subQ5=sQuery(id+"F0.wireOp",EDGE,"E407.MirrorCS");Q43=makeQuery(id+"F0.imprint","IMPRINT",FACE,{"disambiguationData":[TD([[makeQuery(id+"F0.imprint","IMPRINT",EDGE,{"derivedFrom":subQ5}),1.0]])]});}
            var Q44;
            Q44=makeQuery(id+"F0.imprint","IMPRINT",FACE,{"disambiguationData":[TD([[makeQuery(id+"F0.imprint","IMPRINT",EDGE,{"derivedFrom":sQuery(id+"F0.wireOp",EDGE,"E363.MirrorCS")}),1.0]])]});
            var Q45;
            {var subQ5=sQuery(id+"F0.wireOp",EDGE,"E401.MirrorCS");Q45=makeQuery(id+"F0.imprint","IMPRINT",FACE,{"disambiguationData":[TD([[makeQuery(id+"F0.imprint","IMPRINT",EDGE,{"derivedFrom":subQ5}),1.0]])]});}
            var Q46;
            Q46=makeQuery(id+"F0.imprint","IMPRINT",FACE,{"disambiguationData":[TD([[makeQuery(id+"F0.imprint","IMPRINT",EDGE,{"derivedFrom":sQuery(id+"F0.wireOp",EDGE,"E389.MirrorCS")}),1.0]])]});
            var Q47;
            {var subQ5=sQuery(id+"F0.wireOp",EDGE,"E454.MirrorCS");Q47=makeQuery(id+"F0.imprint","IMPRINT",FACE,{"disambiguationData":[TD([[makeQuery(id+"F0.imprint","IMPRINT",EDGE,{"derivedFrom":subQ5}),1.0]])]});}
            var Q48;
            Q48=makeQuery(id+"F0.imprint","IMPRINT",FACE,{"disambiguationData":[TD([[makeQuery(id+"F0.imprint","IMPRINT",EDGE,{"derivedFrom":sQuery(id+"F0.wireOp",EDGE,"E371.MirrorCS")}),1.0]])]});
            var Q49;
            {var subQ5=sQuery(id+"F0.wireOp",EDGE,"E451.MirrorCS");Q49=makeQuery(id+"F0.imprint","IMPRINT",FACE,{"disambiguationData":[TD([[makeQuery(id+"F0.imprint","IMPRINT",EDGE,{"derivedFrom":subQ5}),1.0]])]});}
            var Q50;
            Q50=makeQuery(id+"F0.imprint","IMPRINT",FACE,{"disambiguationData":[TD([[makeQuery(id+"F0.imprint","IMPRINT",EDGE,{"derivedFrom":sQuery(id+"F0.wireOp",EDGE,"E404.MirrorCS")}),1.0]])]});
            var Q51;
            {var subQ5=sQuery(id+"F0.wireOp",EDGE,"E403.MirrorCS");Q51=makeQuery(id+"F0.imprint","IMPRINT",FACE,{"disambiguationData":[TD([[makeQuery(id+"F0.imprint","IMPRINT",EDGE,{"derivedFrom":subQ5}),1.0]])]});}
            var Q52;
            Q52=makeQuery(id+"F0.imprint","IMPRINT",FACE,{"disambiguationData":[TD([[makeQuery(id+"F0.imprint","IMPRINT",EDGE,{"derivedFrom":sQuery(id+"F0.wireOp",EDGE,"E388.MirrorCS")}),1.0]])]});
            var Q53;
            {var subQ5=sQuery(id+"F0.wireOp",EDGE,"E392.MirrorCS");Q53=makeQuery(id+"F0.imprint","IMPRINT",FACE,{"disambiguationData":[TD([[makeQuery(id+"F0.imprint","IMPRINT",EDGE,{"derivedFrom":subQ5}),1.0]])]});}
            var Q54;
            Q54=makeQuery(id+"F0.imprint","IMPRINT",FACE,{"disambiguationData":[TD([[makeQuery(id+"F0.imprint","IMPRINT",EDGE,{"derivedFrom":sQuery(id+"F0.wireOp",EDGE,"E373.MirrorCS")}),1.0]])]});
            var Q55;
            {var subQ5=sQuery(id+"F0.wireOp",EDGE,"E361.MirrorCS");Q55=makeQuery(id+"F0.imprint","IMPRINT",FACE,{"disambiguationData":[TD([[makeQuery(id+"F0.imprint","IMPRINT",EDGE,{"derivedFrom":subQ5}),1.0]])]});}
            var Q56;
            {var subQ6=sQuery(id+"F0.wireOp",EDGE,"E3471.MirrorCS");Q56=makeQuery(id+"F0.imprint","IMPRINT",FACE,{"disambiguationData":[TD([[makeQuery(id+"F0.imprint","IMPRINT",EDGE,{"derivedFrom":subQ6}),1.0]])]});}
            var Q57;
            {var subQ0=sQuery(id+"F0.wireOp",EDGE,"46eebdd7-9ef8-4a30-b2d4-09e9d8da565d4.MirrorCS");var subQ1=sQuery(id+"F0.wireOp",EDGE,"E0");var subQ2=makeQuery(id+"F0.imprint","INTERSECT",VERTEX,{"derivedFrom":[subQ1,subQ0]});Q57=makeQuery(id+"F0.imprint","IMPRINT",FACE,{"disambiguationData":[TD([[makeQuery(id+"F0.imprint","IMPRINT",EDGE,{"disambiguationData":[TD([[subQ2,-1.0]])],"derivedFrom":subQ1}),1.0]])]});}
            var Q58;
            Q58=makeQuery(id+"F0.imprint","IMPRINT",FACE,{"disambiguationData":[TD([[makeQuery(id+"F0.imprint","IMPRINT",EDGE,{"derivedFrom":sQuery(id+"F0.wireOp",EDGE,"E366.MirrorCS")}),-1.0]])]});
            var Q59;
            {var subQ5=sQuery(id+"F0.wireOp",EDGE,"E387.MirrorCS");Q59=makeQuery(id+"F0.imprint","IMPRINT",FACE,{"disambiguationData":[TD([[makeQuery(id+"F0.imprint","IMPRINT",EDGE,{"derivedFrom":subQ5}),-1.0]])]});}
            var Q60;
            Q60=makeQuery(id+"F0.imprint","IMPRINT",FACE,{"disambiguationData":[TD([[makeQuery(id+"F0.imprint","IMPRINT",EDGE,{"derivedFrom":sQuery(id+"F0.wireOp",EDGE,"E379.MirrorCS")}),-1.0]])]});
            var Q61;
            {var subQ5=sQuery(id+"F0.wireOp",EDGE,"E374.MirrorCS");Q61=makeQuery(id+"F0.imprint","IMPRINT",FACE,{"disambiguationData":[TD([[makeQuery(id+"F0.imprint","IMPRINT",EDGE,{"derivedFrom":subQ5}),-1.0]])]});}
            var Q62;
            Q62=makeQuery(id+"F0.imprint","IMPRINT",FACE,{"disambiguationData":[TD([[makeQuery(id+"F0.imprint","IMPRINT",EDGE,{"derivedFrom":sQuery(id+"F0.wireOp",EDGE,"E365.MirrorCS")}),-1.0]])]});
            var Q63;
            {var subQ5=sQuery(id+"F0.wireOp",EDGE,"E380.MirrorCS");Q63=makeQuery(id+"F0.imprint","IMPRINT",FACE,{"disambiguationData":[TD([[makeQuery(id+"F0.imprint","IMPRINT",EDGE,{"derivedFrom":subQ5}),-1.0]])]});}
            var Q64;
            Q64=makeQuery(id+"F0.imprint","IMPRINT",FACE,{"disambiguationData":[TD([[makeQuery(id+"F0.imprint","IMPRINT",EDGE,{"derivedFrom":sQuery(id+"F0.wireOp",EDGE,"E381.MirrorCS")}),-1.0]])]});
            var Q65;
            {var subQ5=sQuery(id+"F0.wireOp",EDGE,"E433.MirrorCS");Q65=makeQuery(id+"F0.imprint","IMPRINT",FACE,{"disambiguationData":[TD([[makeQuery(id+"F0.imprint","IMPRINT",EDGE,{"derivedFrom":subQ5}),-1.0]])]});}
            var Q66;
            Q66=makeQuery(id+"F0.imprint","IMPRINT",FACE,{"disambiguationData":[TD([[makeQuery(id+"F0.imprint","IMPRINT",EDGE,{"derivedFrom":sQuery(id+"F0.wireOp",EDGE,"E397.MirrorCS")}),-1.0]])]});
            var Q67;
            {var subQ5=sQuery(id+"F0.wireOp",EDGE,"E455.MirrorCS");Q67=makeQuery(id+"F0.imprint","IMPRINT",FACE,{"disambiguationData":[TD([[makeQuery(id+"F0.imprint","IMPRINT",EDGE,{"derivedFrom":subQ5}),-1.0]])]});}
            var Q68;
            Q68=makeQuery(id+"F0.imprint","IMPRINT",FACE,{"disambiguationData":[TD([[makeQuery(id+"F0.imprint","IMPRINT",EDGE,{"derivedFrom":sQuery(id+"F0.wireOp",EDGE,"E386.MirrorCS")}),-1.0]])]});
            var Q69;
            {var subQ5=sQuery(id+"F0.wireOp",EDGE,"E393.MirrorCS");Q69=makeQuery(id+"F0.imprint","IMPRINT",FACE,{"disambiguationData":[TD([[makeQuery(id+"F0.imprint","IMPRINT",EDGE,{"derivedFrom":subQ5}),-1.0]])]});}
            var Q70;
            Q70=makeQuery(id+"F0.imprint","IMPRINT",FACE,{"disambiguationData":[TD([[makeQuery(id+"F0.imprint","IMPRINT",EDGE,{"derivedFrom":sQuery(id+"F0.wireOp",EDGE,"E357.MirrorCS")}),-1.0]])]});
            var Q71;
            {var subQ5=sQuery(id+"F0.wireOp",EDGE,"E414.MirrorCS");Q71=makeQuery(id+"F0.imprint","IMPRINT",FACE,{"disambiguationData":[TD([[makeQuery(id+"F0.imprint","IMPRINT",EDGE,{"derivedFrom":subQ5}),-1.0]])]});}
            var Q72;
            Q72=makeQuery(id+"F0.imprint","IMPRINT",FACE,{"disambiguationData":[TD([[makeQuery(id+"F0.imprint","IMPRINT",EDGE,{"derivedFrom":sQuery(id+"F0.wireOp",EDGE,"E358.MirrorCS")}),-1.0]])]});
            var Q73;
            {var subQ5=sQuery(id+"F0.wireOp",EDGE,"E442.MirrorCS");Q73=makeQuery(id+"F0.imprint","IMPRINT",FACE,{"disambiguationData":[TD([[makeQuery(id+"F0.imprint","IMPRINT",EDGE,{"derivedFrom":subQ5}),-1.0]])]});}
            var Q74;
            Q74=makeQuery(id+"F0.imprint","IMPRINT",FACE,{"disambiguationData":[TD([[makeQuery(id+"F0.imprint","IMPRINT",EDGE,{"derivedFrom":sQuery(id+"F0.wireOp",EDGE,"E356.MirrorCS")}),-1.0]])]});
            var Q75;
            {var subQ5=sQuery(id+"F0.wireOp",EDGE,"E399.MirrorCS");Q75=makeQuery(id+"F0.imprint","IMPRINT",FACE,{"disambiguationData":[TD([[makeQuery(id+"F0.imprint","IMPRINT",EDGE,{"derivedFrom":subQ5}),-1.0]])]});}
            var Q76;
            {var subQ0=sQuery(id+"F0.wireOp",EDGE,"E95");Q76=makeQuery(id+"F0.imprint","IMPRINT",FACE,{"disambiguationData":[TD([[makeQuery(id+"F0.imprint","IMPRINT",EDGE,{"derivedFrom":subQ0}),1.0]])]});}
            var Q77;
            {var subQ5=sQuery(id+"F0.wireOp",EDGE,"E94");Q77=makeQuery(id+"F0.imprint","IMPRINT",FACE,{"disambiguationData":[TD([[makeQuery(id+"F0.imprint","IMPRINT",EDGE,{"derivedFrom":subQ5}),1.0]])]});}
            var Q78;
            {var subQ1=sQuery(id+"F0.wireOp",EDGE,"E77");Q78=makeQuery(id+"F0.imprint","IMPRINT",FACE,{"disambiguationData":[TD([[makeQuery(id+"F0.imprint","IMPRINT",EDGE,{"derivedFrom":subQ1}),1.0]])]});}
            var Q79;
            {var subQ5=sQuery(id+"F0.wireOp",EDGE,"E76");Q79=makeQuery(id+"F0.imprint","IMPRINT",FACE,{"disambiguationData":[TD([[makeQuery(id+"F0.imprint","IMPRINT",EDGE,{"derivedFrom":subQ5}),1.0]])]});}
            var Q80;
            {var subQ6=sQuery(id+"F0.wireOp",EDGE,"Ok7nrS8m-fPNG-4Qwz-1IUJ-TIJfWUFwrWGG");Q80=makeQuery(id+"F0.imprint","IMPRINT",FACE,{"disambiguationData":[TD([[makeQuery(id+"F0.imprint","IMPRINT",EDGE,{"derivedFrom":subQ6}),1.0]])]});}
            var Q81;
            {var subQ1=sQuery(id+"F0.wireOp",EDGE,"E13");Q81=makeQuery(id+"F0.imprint","IMPRINT",FACE,{"disambiguationData":[TD([[makeQuery(id+"F0.imprint","IMPRINT",EDGE,{"derivedFrom":subQ1}),1.0]])]});}
            var Q82;
            {var subQ5=sQuery(id+"F0.wireOp",EDGE,"E4");Q82=makeQuery(id+"F0.imprint","IMPRINT",FACE,{"disambiguationData":[TD([[makeQuery(id+"F0.imprint","IMPRINT",EDGE,{"derivedFrom":subQ5}),1.0]])]});}
            var Q83;
            {var subQ1=sQuery(id+"F0.wireOp",EDGE,"E5");Q83=makeQuery(id+"F0.imprint","IMPRINT",FACE,{"disambiguationData":[TD([[makeQuery(id+"F0.imprint","IMPRINT",EDGE,{"derivedFrom":subQ1}),1.0]])]});}
            var Q84;
            {var subQ3=sQuery(id+"F0.wireOp",EDGE,"E346.MirrorCS");Q84=makeQuery(id+"F0.imprint","IMPRINT",FACE,{"disambiguationData":[TD([[makeQuery(id+"F0.imprint","IMPRINT",EDGE,{"derivedFrom":subQ3}),1.0]])]});}
            var Q85;
            {var subQ1=sQuery(id+"F0.wireOp",EDGE,"E347.MirrorCS");Q85=makeQuery(id+"F0.imprint","IMPRINT",FACE,{"disambiguationData":[TD([[makeQuery(id+"F0.imprint","IMPRINT",EDGE,{"derivedFrom":subQ1}),1.0]])]});}
            extrude(context, id + "F2", {"entities" : qUnion([Q0, Q1, Q2, Q3, Q4, Q5, Q6, Q7, Q8, Q9, Q10, Q11, Q12, Q13, Q14, Q15, Q16, Q17, Q18, Q19, Q20, Q21, Q22, Q23, Q24, Q25, Q26, Q27, Q28, Q29, Q30, Q31, Q32, Q33, Q34, Q35, Q36, Q37, Q38, Q39, Q40, Q41, Q42, Q43, Q44, Q45, Q46, Q47, Q48, Q49, Q50, Q51, Q52, Q53, Q54, Q55, Q56, Q57, Q58, Q59, Q60, Q61, Q62, Q63, Q64, Q65, Q66, Q67, Q68, Q69, Q70, Q71, Q72, Q73, Q74, Q75, Q76, Q77, Q78, Q79, Q80, Q81, Q82, Q83, Q84, Q85]), "depth" : 12.7 * mm});
        }
        {
            var Q0;
            Q0=makeQuery(id+"F0.imprint","IMPRINT",FACE,{"disambiguationData":[TD([[makeQuery(id+"F0.imprint","IMPRINT",EDGE,{"derivedFrom":sQuery(id+"F0.wireOp",EDGE,"E514")}),-1.0]])]});
            var Q1;
            {var subQ6=sQuery(id+"F0.wireOp",EDGE,"E596");Q1=makeQuery(id+"F0.imprint","IMPRINT",FACE,{"disambiguationData":[TD([[makeQuery(id+"F0.imprint","IMPRINT",EDGE,{"derivedFrom":subQ6}),1.0]])]});}
            var Q2;
            Q2=makeQuery(id+"F0.imprint","IMPRINT",FACE,{"disambiguationData":[TD([[makeQuery(id+"F0.imprint","IMPRINT",EDGE,{"derivedFrom":sQuery(id+"F0.wireOp",EDGE,"E572.MirrorCS")}),-1.0]])]});
            var Q3;
            Q3=makeQuery(id+"F0.imprint","IMPRINT",FACE,{"disambiguationData":[TD([[makeQuery(id+"F0.imprint","IMPRINT",EDGE,{"derivedFrom":sQuery(id+"F0.wireOp",EDGE,"E566.MirrorCS")}),-1.0]])]});
            var Q4;
            Q4=makeQuery(id+"F0.imprint","IMPRINT",FACE,{"disambiguationData":[TD([[makeQuery(id+"F0.imprint","IMPRINT",EDGE,{"derivedFrom":sQuery(id+"F0.wireOp",EDGE,"E564.MirrorCS")}),-1.0]])]});
            var Q5;
            Q5=makeQuery(id+"F0.imprint","IMPRINT",FACE,{"disambiguationData":[TD([[makeQuery(id+"F0.imprint","IMPRINT",EDGE,{"derivedFrom":sQuery(id+"F0.wireOp",EDGE,"E563.MirrorCS")}),-1.0]])]});
            var Q6;
            Q6=makeQuery(id+"F0.imprint","IMPRINT",FACE,{"disambiguationData":[TD([[makeQuery(id+"F0.imprint","IMPRINT",EDGE,{"derivedFrom":sQuery(id+"F0.wireOp",EDGE,"E603.MirrorCS")}),1.0]])]});
            var Q7;
            Q7=makeQuery(id+"F0.imprint","IMPRINT",FACE,{"disambiguationData":[TD([[makeQuery(id+"F0.imprint","IMPRINT",EDGE,{"derivedFrom":sQuery(id+"F0.wireOp",EDGE,"E608.MirrorCS")}),1.0]])]});
            var Q8;
            Q8=makeQuery(id+"F0.imprint","IMPRINT",FACE,{"disambiguationData":[TD([[makeQuery(id+"F0.imprint","IMPRINT",EDGE,{"derivedFrom":sQuery(id+"F0.wireOp",EDGE,"E609.MirrorCS")}),1.0]])]});
            var Q9;
            Q9=makeQuery(id+"F0.imprint","IMPRINT",FACE,{"disambiguationData":[TD([[makeQuery(id+"F0.imprint","IMPRINT",EDGE,{"derivedFrom":sQuery(id+"F0.wireOp",EDGE,"E607.MirrorCS")}),-1.0]])]});
            var Q10;
            Q10=makeQuery(id+"F0.imprint","IMPRINT",FACE,{"disambiguationData":[TD([[makeQuery(id+"F0.imprint","IMPRINT",EDGE,{"derivedFrom":sQuery(id+"F0.wireOp",EDGE,"E606.MirrorCS")}),-1.0]])]});
            var Q11;
            Q11=makeQuery(id+"F0.imprint","IMPRINT",FACE,{"disambiguationData":[TD([[makeQuery(id+"F0.imprint","IMPRINT",EDGE,{"derivedFrom":sQuery(id+"F0.wireOp",EDGE,"E611.MirrorCS")}),-1.0]])]});
            var Q12;
            Q12=makeQuery(id+"F0.imprint","IMPRINT",FACE,{"disambiguationData":[TD([[makeQuery(id+"F0.imprint","IMPRINT",EDGE,{"derivedFrom":sQuery(id+"F0.wireOp",EDGE,"E605.MirrorCS")}),-1.0]])]});
            var Q13;
            Q13=makeQuery(id+"F0.imprint","IMPRINT",FACE,{"disambiguationData":[TD([[makeQuery(id+"F0.imprint","IMPRINT",EDGE,{"derivedFrom":sQuery(id+"F0.wireOp",EDGE,"E610.MirrorCS")}),-1.0]])]});
            var Q14;
            Q14=makeQuery(id+"F0.imprint","IMPRINT",FACE,{"disambiguationData":[TD([[makeQuery(id+"F0.imprint","IMPRINT",EDGE,{"derivedFrom":sQuery(id+"F0.wireOp",EDGE,"E604.MirrorCS")}),-1.0]])]});
            var Q15;
            {var subQ0=sQuery(id+"F0.wireOp",EDGE,"E556");Q15=makeQuery(id+"F0.imprint","IMPRINT",FACE,{"disambiguationData":[TD([[makeQuery(id+"F0.imprint","IMPRINT",EDGE,{"derivedFrom":subQ0}),1.0]])]});}
            var Q16;
            {var subQ1=sQuery(id+"F0.wireOp",EDGE,"E548");Q16=makeQuery(id+"F0.imprint","IMPRINT",FACE,{"disambiguationData":[TD([[makeQuery(id+"F0.imprint","IMPRINT",EDGE,{"derivedFrom":subQ1}),1.0]])]});}
            var Q17;
            {var subQ1=sQuery(id+"F0.wireOp",EDGE,"E540");Q17=makeQuery(id+"F0.imprint","IMPRINT",FACE,{"disambiguationData":[TD([[makeQuery(id+"F0.imprint","IMPRINT",EDGE,{"derivedFrom":subQ1}),1.0]])]});}
            var Q18;
            {var subQ1=sQuery(id+"F0.wireOp",EDGE,"E532");Q18=makeQuery(id+"F0.imprint","IMPRINT",FACE,{"disambiguationData":[TD([[makeQuery(id+"F0.imprint","IMPRINT",EDGE,{"derivedFrom":subQ1}),1.0]])]});}
            var Q19;
            {var subQ1=sQuery(id+"F0.wireOp",EDGE,"E524");Q19=makeQuery(id+"F0.imprint","IMPRINT",FACE,{"disambiguationData":[TD([[makeQuery(id+"F0.imprint","IMPRINT",EDGE,{"derivedFrom":subQ1}),1.0]])]});}
            var Q20;
            {var subQ0=sQuery(id+"F0.wireOp",EDGE,"E516");Q20=makeQuery(id+"F0.imprint","IMPRINT",FACE,{"disambiguationData":[TD([[makeQuery(id+"F0.imprint","IMPRINT",EDGE,{"derivedFrom":subQ0}),1.0]])]});}
            var Q21;
            {var subQ5=sQuery(id+"F0.wireOp",EDGE,"E515");Q21=makeQuery(id+"F0.imprint","IMPRINT",FACE,{"disambiguationData":[TD([[makeQuery(id+"F0.imprint","IMPRINT",EDGE,{"derivedFrom":subQ5}),1.0]])]});}
            var Q22;
            {var subQ5=sQuery(id+"F0.wireOp",EDGE,"E595");Q22=makeQuery(id+"F0.imprint","IMPRINT",FACE,{"disambiguationData":[TD([[makeQuery(id+"F0.imprint","IMPRINT",EDGE,{"derivedFrom":subQ5}),1.0]])]});}
            var Q23;
            {var subQ5=sQuery(id+"F0.wireOp",EDGE,"E570.MirrorCS");Q23=makeQuery(id+"F0.imprint","IMPRINT",FACE,{"disambiguationData":[TD([[makeQuery(id+"F0.imprint","IMPRINT",EDGE,{"derivedFrom":subQ5}),-1.0]])]});}
            var Q24;
            {var subQ5=sQuery(id+"F0.wireOp",EDGE,"E581.MirrorCS");Q24=makeQuery(id+"F0.imprint","IMPRINT",FACE,{"disambiguationData":[TD([[makeQuery(id+"F0.imprint","IMPRINT",EDGE,{"derivedFrom":subQ5}),-1.0]])]});}
            var Q25;
            {var subQ5=sQuery(id+"F0.wireOp",EDGE,"E571.MirrorCS");Q25=makeQuery(id+"F0.imprint","IMPRINT",FACE,{"disambiguationData":[TD([[makeQuery(id+"F0.imprint","IMPRINT",EDGE,{"derivedFrom":subQ5}),-1.0]])]});}
            var Q26;
            {var subQ5=sQuery(id+"F0.wireOp",EDGE,"E582.MirrorCS");Q26=makeQuery(id+"F0.imprint","IMPRINT",FACE,{"disambiguationData":[TD([[makeQuery(id+"F0.imprint","IMPRINT",EDGE,{"derivedFrom":subQ5}),-1.0]])]});}
            var Q27;
            {var subQ5=sQuery(id+"F0.wireOp",EDGE,"E655.MirrorCS");Q27=makeQuery(id+"F0.imprint","IMPRINT",FACE,{"disambiguationData":[TD([[makeQuery(id+"F0.imprint","IMPRINT",EDGE,{"derivedFrom":subQ5}),1.0]])]});}
            var Q28;
            {var subQ5=sQuery(id+"F0.wireOp",EDGE,"E627.MirrorCS");Q28=makeQuery(id+"F0.imprint","IMPRINT",FACE,{"disambiguationData":[TD([[makeQuery(id+"F0.imprint","IMPRINT",EDGE,{"derivedFrom":subQ5}),1.0]])]});}
            var Q29;
            {var subQ5=sQuery(id+"F0.wireOp",EDGE,"E649.MirrorCS");Q29=makeQuery(id+"F0.imprint","IMPRINT",FACE,{"disambiguationData":[TD([[makeQuery(id+"F0.imprint","IMPRINT",EDGE,{"derivedFrom":subQ5}),1.0]])]});}
            var Q30;
            {var subQ5=sQuery(id+"F0.wireOp",EDGE,"E621.MirrorCS");Q30=makeQuery(id+"F0.imprint","IMPRINT",FACE,{"disambiguationData":[TD([[makeQuery(id+"F0.imprint","IMPRINT",EDGE,{"derivedFrom":subQ5}),-1.0]])]});}
            var Q31;
            {var subQ5=sQuery(id+"F0.wireOp",EDGE,"E619.MirrorCS");Q31=makeQuery(id+"F0.imprint","IMPRINT",FACE,{"disambiguationData":[TD([[makeQuery(id+"F0.imprint","IMPRINT",EDGE,{"derivedFrom":subQ5}),-1.0]])]});}
            var Q32;
            {var subQ5=sQuery(id+"F0.wireOp",EDGE,"E654.MirrorCS");Q32=makeQuery(id+"F0.imprint","IMPRINT",FACE,{"disambiguationData":[TD([[makeQuery(id+"F0.imprint","IMPRINT",EDGE,{"derivedFrom":subQ5}),-1.0]])]});}
            var Q33;
            {var subQ5=sQuery(id+"F0.wireOp",EDGE,"E618.MirrorCS");Q33=makeQuery(id+"F0.imprint","IMPRINT",FACE,{"disambiguationData":[TD([[makeQuery(id+"F0.imprint","IMPRINT",EDGE,{"derivedFrom":subQ5}),-1.0]])]});}
            var Q34;
            {var subQ5=sQuery(id+"F0.wireOp",EDGE,"E653.MirrorCS");Q34=makeQuery(id+"F0.imprint","IMPRINT",FACE,{"disambiguationData":[TD([[makeQuery(id+"F0.imprint","IMPRINT",EDGE,{"derivedFrom":subQ5}),-1.0]])]});}
            var Q35;
            {var subQ5=sQuery(id+"F0.wireOp",EDGE,"E617.MirrorCS");Q35=makeQuery(id+"F0.imprint","IMPRINT",FACE,{"disambiguationData":[TD([[makeQuery(id+"F0.imprint","IMPRINT",EDGE,{"derivedFrom":subQ5}),-1.0]])]});}
            var Q36;
            {var subQ5=sQuery(id+"F0.wireOp",EDGE,"E555");Q36=makeQuery(id+"F0.imprint","IMPRINT",FACE,{"disambiguationData":[TD([[makeQuery(id+"F0.imprint","IMPRINT",EDGE,{"derivedFrom":subQ5}),1.0]])]});}
            var Q37;
            {var subQ5=sQuery(id+"F0.wireOp",EDGE,"E547");Q37=makeQuery(id+"F0.imprint","IMPRINT",FACE,{"disambiguationData":[TD([[makeQuery(id+"F0.imprint","IMPRINT",EDGE,{"derivedFrom":subQ5}),1.0]])]});}
            var Q38;
            {var subQ5=sQuery(id+"F0.wireOp",EDGE,"E539");Q38=makeQuery(id+"F0.imprint","IMPRINT",FACE,{"disambiguationData":[TD([[makeQuery(id+"F0.imprint","IMPRINT",EDGE,{"derivedFrom":subQ5}),1.0]])]});}
            var Q39;
            {var subQ5=sQuery(id+"F0.wireOp",EDGE,"E531");Q39=makeQuery(id+"F0.imprint","IMPRINT",FACE,{"disambiguationData":[TD([[makeQuery(id+"F0.imprint","IMPRINT",EDGE,{"derivedFrom":subQ5}),1.0]])]});}
            var Q40;
            {var subQ5=sQuery(id+"F0.wireOp",EDGE,"E523");Q40=makeQuery(id+"F0.imprint","IMPRINT",FACE,{"disambiguationData":[TD([[makeQuery(id+"F0.imprint","IMPRINT",EDGE,{"derivedFrom":subQ5}),1.0]])]});}
            extrude(context, id + "F3", {"entities" : qUnion([Q0, Q1, Q2, Q3, Q4, Q5, Q6, Q7, Q8, Q9, Q10, Q11, Q12, Q13, Q14, Q15, Q16, Q17, Q18, Q19, Q20, Q21, Q22, Q23, Q24, Q25, Q26, Q27, Q28, Q29, Q30, Q31, Q32, Q33, Q34, Q35, Q36, Q37, Q38, Q39, Q40]), "depth" : 6.35 * mm});
        }
    });
